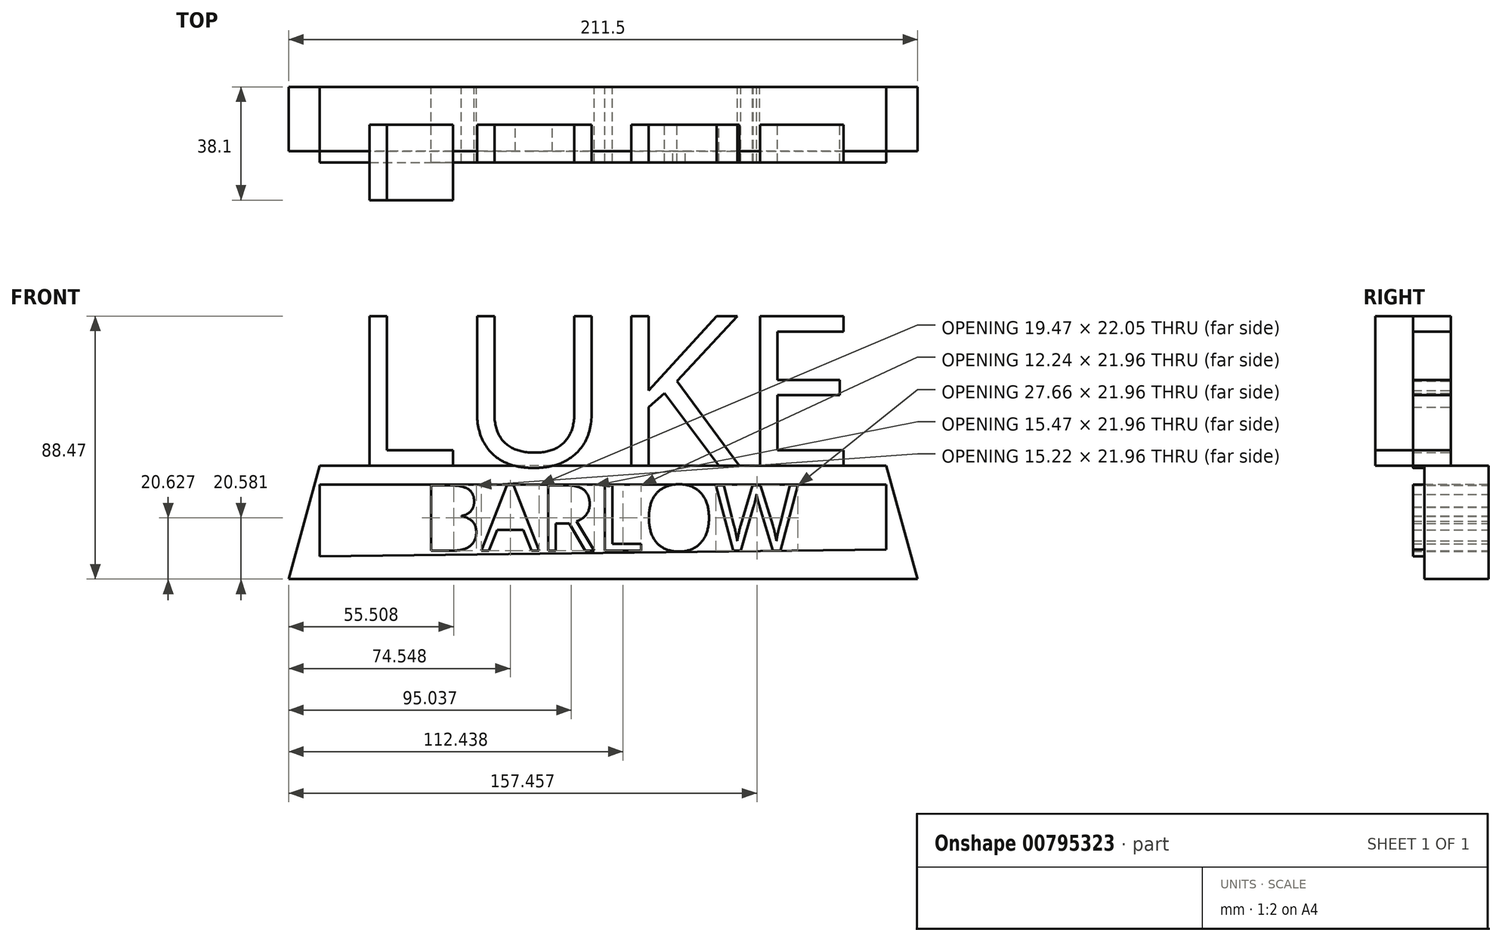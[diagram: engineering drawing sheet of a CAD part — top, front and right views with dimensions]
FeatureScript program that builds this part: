
annotation { "Feature Type Name" : "Feature", "Feature Type Description" : "" }
export const myFeature = defineFeature(function(context is Context, id is Id, definition is map)
    precondition{}
    {
        {
            var Q0;
            Q0=qCreatedBy(makeId("Front.planeOp"),FACE);
            var sketch = newSketch(context, id + "F0", { "sketchPlane" : qUnion([Q0])});
            skText(sketch, "E0", { "text": "LUKE\n", "fontName": "OpenSans-Regular.ttf"});
            skLineSegment(sketch, "E1.bottom", {"start": v(95.25, 0) * mm, "end": v(-95.25, 0) * mm});
            skLineSegment(sketch, "E1.top", {"start": v(95.25, -38.1) * mm, "end": v(-95.25, -38.1) * mm});
            skLineSegment(sketch, "E1.left", {"start": v(95.25, -6.35) * mm, "end": v(95.25, -28.18) * mm});
            skLineSegment(sketch, "E1.right", {"start": v(-95.25, -6.35) * mm, "end": v(-95.25, -30.4) * mm});
            skPoint(sketch, "E1.middle", {"position": v(0, -19.05) * mm});
            skLineSegment(sketch, "E2", {"start": v(-95.25, -6.35) * mm, "end": v(95.25, -6.35) * mm});
            skLineSegment(sketch, "E3.MirrorCS", {"start": v(-95.25, -30.4) * mm, "end": v(95.25, -28.18) * mm});
            skPoint(sketch, "E4.orphan", {"position": v(-95.25, -19.05) * mm});
            skPoint(sketch, "E5.end.orphan", {"position": v(95.25, -19.05) * mm});
            skLineSegment(sketch, "E6", {"start": v(-95.25, 0) * mm, "end": v(-105.75, -38.1) * mm});
            skLineSegment(sketch, "E7", {"start": v(-105.75, -38.1) * mm, "end": v(-95.25, -38.1) * mm});
            skLineSegment(sketch, "E8.MirrorCS", {"start": v(105.75, -38.1) * mm, "end": v(95.25, -38.1) * mm});
            skLineSegment(sketch, "E9.MirrorCS", {"start": v(95.25, 0) * mm, "end": v(105.75, -38.1) * mm});
            skText(sketch, "E10", { "text": "BARLOW", "fontName": "OpenSans-Regular.ttf"});
            const initialGuessF0  = {"E0": [-0.08543, 0, 1, 0, 0.0508], "E10": [-0.06087, -0.0285, 1, 0, 0.02215]};
            skSetInitialGuess(sketch, initialGuessF0);
            skSolve(sketch);
        }
        {
            var Q0;
            Q0=qSketchRegion(id+"F0",true);
            var Q1;
            Q1=makeQuery(id+"F0.imprint","IMPRINT",FACE,{"disambiguationData":[TD([[makeQuery(id+"F0.imprint","IMPRINT",EDGE,{"derivedFrom":sQuery(id+"F0.wireOp",EDGE,"63b13505-105a-406d-b1b1-810f40fcbeff.sketch_text.stroke-0")}),-1.0]])]});
            var Q2;
            {var subQ0=sQuery(id+"F0.wireOp",EDGE,"63b13505-105a-406d-b1b1-810f40fcbeff.sketch_text.stroke-1");Q2=makeQuery(id+"F0.imprint","IMPRINT",FACE,{"disambiguationData":[TD([[makeQuery(id+"F0.imprint","IMPRINT",EDGE,{"derivedFrom":subQ0}),1.0]])]});}
            var Q3;
            {var subQ29=sQuery(id+"F0.wireOp",EDGE,"E1.right");Q3=makeQuery(id+"F0.imprint","IMPRINT",FACE,{"disambiguationData":[TD([[makeQuery(id+"F0.imprint","IMPRINT",EDGE,{"derivedFrom":subQ29}),1.0]])]});}
            var Q4;
            {var subQ6=sQuery(id+"F0.wireOp",EDGE,"63b13505-105a-406d-b1b1-810f40fcbeff.sketch_text.stroke-29");Q4=makeQuery(id+"F0.imprint","IMPRINT",FACE,{"disambiguationData":[TD([[makeQuery(id+"F0.imprint","IMPRINT",EDGE,{"derivedFrom":subQ6}),-1.0]])]});}
            var Q5;
            {var subQ0=sQuery(id+"F0.wireOp",EDGE,"63b13505-105a-406d-b1b1-810f40fcbeff.sketch_text.stroke-31");var subQ1=sQuery(id+"F0.wireOp",EDGE,"E3.MirrorCS");var subQ2=makeQuery(id+"F0.imprint","INTERSECT",VERTEX,{"derivedFrom":[subQ1,subQ0]});Q5=makeQuery(id+"F0.imprint","IMPRINT",FACE,{"disambiguationData":[TD([[makeQuery(id+"F0.imprint","IMPRINT",EDGE,{"disambiguationData":[TD([[subQ2,-1.0]])],"derivedFrom":subQ1}),-1.0]])]});}
            var Q6;
            Q6=makeQuery(id+"F0.imprint","IMPRINT",FACE,{"disambiguationData":[TD([[makeQuery(id+"F0.imprint","IMPRINT",EDGE,{"derivedFrom":sQuery(id+"F0.wireOp",EDGE,"63b13505-105a-406d-b1b1-810f40fcbeff.sketch_text.stroke-38")}),1.0]])]});
            var Q7;
            Q7=makeQuery(id+"F0.imprint","IMPRINT",FACE,{"disambiguationData":[TD([[makeQuery(id+"F0.imprint","IMPRINT",EDGE,{"derivedFrom":sQuery(id+"F0.wireOp",EDGE,"63b13505-105a-406d-b1b1-810f40fcbeff.sketch_text.stroke-21")}),1.0]])]});
            var Q8;
            {var subQ6=sQuery(id+"F0.wireOp",EDGE,"63b13505-105a-406d-b1b1-810f40fcbeff.sketch_text.stroke-12");Q8=makeQuery(id+"F0.imprint","IMPRINT",FACE,{"disambiguationData":[TD([[makeQuery(id+"F0.imprint","IMPRINT",EDGE,{"derivedFrom":subQ6}),-1.0]])]});}
            var Q9;
            {var subQ0=sQuery(id+"F0.wireOp",EDGE,"63b13505-105a-406d-b1b1-810f40fcbeff.sketch_text.stroke-14");var subQ1=sQuery(id+"F0.wireOp",EDGE,"E3.MirrorCS");var subQ2=makeQuery(id+"F0.imprint","INTERSECT",VERTEX,{"derivedFrom":[subQ1,subQ0]});Q9=makeQuery(id+"F0.imprint","IMPRINT",FACE,{"disambiguationData":[TD([[makeQuery(id+"F0.imprint","IMPRINT",EDGE,{"disambiguationData":[TD([[subQ2,-1.0]])],"derivedFrom":subQ1}),-1.0]])]});}
            var Q10;
            Q10=makeQuery(id+"F0.imprint","IMPRINT",FACE,{"disambiguationData":[TD([[makeQuery(id+"F0.imprint","IMPRINT",EDGE,{"derivedFrom":sQuery(id+"F0.wireOp",EDGE,"63b13505-105a-406d-b1b1-810f40fcbeff.sketch_text.stroke-84")}),1.0]])]});
            var Q11;
            Q11=makeQuery(id+"F0.imprint","IMPRINT",FACE,{"disambiguationData":[TD([[makeQuery(id+"F0.imprint","IMPRINT",EDGE,{"derivedFrom":sQuery(id+"F0.wireOp",EDGE,"63b13505-105a-406d-b1b1-810f40fcbeff.sketch_text.stroke-46")}),-1.0]])]});
            var Q12;
            {var subQ5=sQuery(id+"F0.wireOp",EDGE,"63b13505-105a-406d-b1b1-810f40fcbeff.sketch_text.stroke-81");Q12=makeQuery(id+"F0.imprint","IMPRINT",FACE,{"disambiguationData":[TD([[makeQuery(id+"F0.imprint","IMPRINT",EDGE,{"derivedFrom":subQ5}),1.0]])]});}
            var Q13;
            Q13=makeQuery(id+"F0.imprint","IMPRINT",FACE,{"disambiguationData":[TD([[makeQuery(id+"F0.imprint","IMPRINT",EDGE,{"derivedFrom":sQuery(id+"F0.wireOp",EDGE,"63b13505-105a-406d-b1b1-810f40fcbeff.sketch_text.stroke-75")}),1.0]])]});
            var Q14;
            {var subQ11=sQuery(id+"F0.wireOp",EDGE,"63b13505-105a-406d-b1b1-810f40fcbeff.sketch_text.stroke-59");Q14=makeQuery(id+"F0.imprint","IMPRINT",FACE,{"disambiguationData":[TD([[makeQuery(id+"F0.imprint","IMPRINT",EDGE,{"derivedFrom":subQ11}),-1.0]])]});}
            var Q15;
            Q15=makeQuery(id+"F0.imprint","IMPRINT",FACE,{"disambiguationData":[TD([[makeQuery(id+"F0.imprint","IMPRINT",EDGE,{"derivedFrom":sQuery(id+"F0.wireOp",EDGE,"63b13505-105a-406d-b1b1-810f40fcbeff.sketch_text.stroke-104")}),1.0]])]});
            var Q16;
            {var subQ5=sQuery(id+"F0.wireOp",EDGE,"63b13505-105a-406d-b1b1-810f40fcbeff.sketch_text.stroke-91");Q16=makeQuery(id+"F0.imprint","IMPRINT",FACE,{"disambiguationData":[TD([[makeQuery(id+"F0.imprint","IMPRINT",EDGE,{"derivedFrom":subQ5}),-1.0]])]});}
            var Q17;
            {var subQ5=sQuery(id+"F0.wireOp",EDGE,"63b13505-105a-406d-b1b1-810f40fcbeff.sketch_text.stroke-103");Q17=makeQuery(id+"F0.imprint","IMPRINT",FACE,{"disambiguationData":[TD([[makeQuery(id+"F0.imprint","IMPRINT",EDGE,{"derivedFrom":subQ5}),-1.0]])]});}
            var Q18;
            {var subQ0=sQuery(id+"F0.wireOp",EDGE,"63b13505-105a-406d-b1b1-810f40fcbeff.sketch_text.stroke-109");Q18=makeQuery(id+"F0.imprint","IMPRINT",FACE,{"disambiguationData":[TD([[makeQuery(id+"F0.imprint","IMPRINT",EDGE,{"derivedFrom":subQ0}),1.0]])]});}
            var Q19;
            Q19=makeQuery(id+"F0.imprint","IMPRINT",FACE,{"disambiguationData":[TD([[makeQuery(id+"F0.imprint","IMPRINT",EDGE,{"derivedFrom":sQuery(id+"F0.wireOp",EDGE,"63b13505-105a-406d-b1b1-810f40fcbeff.sketch_text.stroke-109")}),-1.0]])]});
            var Q20;
            {var subQ9=sQuery(id+"F0.wireOp",EDGE,"63b13505-105a-406d-b1b1-810f40fcbeff.sketch_text.stroke-126");Q20=makeQuery(id+"F0.imprint","IMPRINT",FACE,{"disambiguationData":[TD([[makeQuery(id+"F0.imprint","IMPRINT",EDGE,{"derivedFrom":subQ9}),-1.0]])]});}
            var Q21;
            Q21=makeQuery(id+"F0.imprint","IMPRINT",FACE,{"disambiguationData":[TD([[makeQuery(id+"F0.imprint","IMPRINT",EDGE,{"derivedFrom":sQuery(id+"F0.wireOp",EDGE,"63b13505-105a-406d-b1b1-810f40fcbeff.sketch_text.stroke-141")}),1.0]])]});
            var Q22;
            {var subQ4=sQuery(id+"F0.wireOp",EDGE,"63b13505-105a-406d-b1b1-810f40fcbeff.sketch_text.stroke-126");Q22=makeQuery(id+"F0.imprint","IMPRINT",FACE,{"disambiguationData":[TD([[makeQuery(id+"F0.imprint","IMPRINT",EDGE,{"derivedFrom":subQ4}),1.0]])]});}
            var Q23;
            {var subQ5=sQuery(id+"F0.wireOp",EDGE,"63b13505-105a-406d-b1b1-810f40fcbeff.sketch_text.stroke-137");Q23=makeQuery(id+"F0.imprint","IMPRINT",FACE,{"disambiguationData":[TD([[makeQuery(id+"F0.imprint","IMPRINT",EDGE,{"derivedFrom":subQ5}),-1.0]])]});}
            var Q24;
            {var subQ0=sQuery(id+"F0.wireOp",EDGE,"63b13505-105a-406d-b1b1-810f40fcbeff.sketch_text.stroke-128");var subQ1=sQuery(id+"F0.wireOp",EDGE,"E3.MirrorCS");var subQ2=makeQuery(id+"F0.imprint","INTERSECT",VERTEX,{"derivedFrom":[subQ1,subQ0]});Q24=makeQuery(id+"F0.imprint","IMPRINT",FACE,{"disambiguationData":[TD([[makeQuery(id+"F0.imprint","IMPRINT",EDGE,{"disambiguationData":[TD([[subQ2,-1.0]])],"derivedFrom":subQ1}),-1.0]])]});}
            var Q25;
            Q25=makeQuery(id+"F0.imprint","IMPRINT",FACE,{"disambiguationData":[TD([[makeQuery(id+"F0.imprint","IMPRINT",EDGE,{"derivedFrom":sQuery(id+"F0.wireOp",EDGE,"63b13505-105a-406d-b1b1-810f40fcbeff.sketch_text.stroke-159")}),1.0]])]});
            var Q26;
            {var subQ6=sQuery(id+"F0.wireOp",EDGE,"63b13505-105a-406d-b1b1-810f40fcbeff.sketch_text.stroke-150");Q26=makeQuery(id+"F0.imprint","IMPRINT",FACE,{"disambiguationData":[TD([[makeQuery(id+"F0.imprint","IMPRINT",EDGE,{"derivedFrom":subQ6}),-1.0]])]});}
            var Q27;
            {var subQ3=sQuery(id+"F0.wireOp",EDGE,"E1.left");Q27=makeQuery(id+"F0.imprint","IMPRINT",FACE,{"disambiguationData":[TD([[makeQuery(id+"F0.imprint","IMPRINT",EDGE,{"derivedFrom":subQ3}),-1.0]])]});}
            var Q28;
            Q28=makeQuery(id+"F0.imprint","IMPRINT",FACE,{"disambiguationData":[TD([[makeQuery(id+"F0.imprint","IMPRINT",EDGE,{"derivedFrom":sQuery(id+"F0.wireOp",EDGE,"63b13505-105a-406d-b1b1-810f40fcbeff.sketch_text.stroke-176")}),1.0]])]});
            var Q29;
            {var subQ6=sQuery(id+"F0.wireOp",EDGE,"63b13505-105a-406d-b1b1-810f40fcbeff.sketch_text.stroke-167");Q29=makeQuery(id+"F0.imprint","IMPRINT",FACE,{"disambiguationData":[TD([[makeQuery(id+"F0.imprint","IMPRINT",EDGE,{"derivedFrom":subQ6}),-1.0]])]});}
            var Q30;
            {var subQ0=sQuery(id+"F0.wireOp",EDGE,"63b13505-105a-406d-b1b1-810f40fcbeff.sketch_text.stroke-169");var subQ1=sQuery(id+"F0.wireOp",EDGE,"E3.MirrorCS");var subQ2=makeQuery(id+"F0.imprint","INTERSECT",VERTEX,{"derivedFrom":[subQ1,subQ0]});Q30=makeQuery(id+"F0.imprint","IMPRINT",FACE,{"disambiguationData":[TD([[makeQuery(id+"F0.imprint","IMPRINT",EDGE,{"disambiguationData":[TD([[subQ2,-1.0]])],"derivedFrom":subQ1}),-1.0]])]});}
            var Q31;
            {var subQ0=sQuery(id+"F0.wireOp",EDGE,"63b13505-105a-406d-b1b1-810f40fcbeff.sketch_text.stroke-152");var subQ1=sQuery(id+"F0.wireOp",EDGE,"E3.MirrorCS");var subQ2=makeQuery(id+"F0.imprint","INTERSECT",VERTEX,{"derivedFrom":[subQ1,subQ0]});Q31=makeQuery(id+"F0.imprint","IMPRINT",FACE,{"disambiguationData":[TD([[makeQuery(id+"F0.imprint","IMPRINT",EDGE,{"disambiguationData":[TD([[subQ2,-1.0]])],"derivedFrom":subQ1}),-1.0]])]});}
            var Q32;
            Q32=makeQuery(id+"F0.imprint","IMPRINT",FACE,{"disambiguationData":[TD([[makeQuery(id+"F0.imprint","IMPRINT",EDGE,{"derivedFrom":sQuery(id+"F0.wireOp",EDGE,"63b13505-105a-406d-b1b1-810f40fcbeff.sketch_text.stroke-184")}),-1.0]])]});
            var Q33;
            {var subQ0=sQuery(id+"F0.wireOp",EDGE,"63b13505-105a-406d-b1b1-810f40fcbeff.sketch_text.stroke-197");Q33=makeQuery(id+"F0.imprint","IMPRINT",FACE,{"disambiguationData":[TD([[makeQuery(id+"F0.imprint","IMPRINT",EDGE,{"derivedFrom":subQ0}),1.0]])]});}
            var Q34;
            Q34=makeQuery(id+"F0.imprint","IMPRINT",FACE,{"disambiguationData":[TD([[makeQuery(id+"F0.imprint","IMPRINT",EDGE,{"derivedFrom":sQuery(id+"F0.wireOp",EDGE,"63b13505-105a-406d-b1b1-810f40fcbeff.sketch_text.stroke-197")}),-1.0]])]});
            extrude(context, id + "F1", {"entities" : qUnion([Q0, Q1, Q2, Q3, Q4, Q5, Q6, Q7, Q8, Q9, Q10, Q11, Q12, Q13, Q14, Q15, Q16, Q17, Q18, Q19, Q20, Q21, Q22, Q23, Q24, Q25, Q26, Q27, Q28, Q29, Q30, Q31, Q32, Q33, Q34]), "depth" : 25.4 * mm, "offsetDistance" : 25.4 * mm});
        }
        {
            var Q0;
            {var subQ6=sQuery(id+"F0.wireOp",EDGE,"63b13505-105a-406d-b1b1-810f40fcbeff.sketch_text.stroke-12");Q0=makeQuery(id+"F0.imprint","IMPRINT",FACE,{"disambiguationData":[TD([[makeQuery(id+"F0.imprint","IMPRINT",EDGE,{"derivedFrom":subQ6}),-1.0]])]});}
            var Q1;
            Q1=makeQuery(id+"F0.imprint","IMPRINT",FACE,{"disambiguationData":[TD([[makeQuery(id+"F0.imprint","IMPRINT",EDGE,{"derivedFrom":sQuery(id+"F0.wireOp",EDGE,"63b13505-105a-406d-b1b1-810f40fcbeff.sketch_text.stroke-0")}),-1.0]])]});
            var Q2;
            {var subQ0=sQuery(id+"F0.wireOp",EDGE,"63b13505-105a-406d-b1b1-810f40fcbeff.sketch_text.stroke-14");var subQ1=sQuery(id+"F0.wireOp",EDGE,"E3.MirrorCS");var subQ2=makeQuery(id+"F0.imprint","INTERSECT",VERTEX,{"derivedFrom":[subQ1,subQ0]});Q2=makeQuery(id+"F0.imprint","IMPRINT",FACE,{"disambiguationData":[TD([[makeQuery(id+"F0.imprint","IMPRINT",EDGE,{"disambiguationData":[TD([[subQ2,-1.0]])],"derivedFrom":subQ1}),-1.0]])]});}
            var Q3;
            {var subQ6=sQuery(id+"F0.wireOp",EDGE,"63b13505-105a-406d-b1b1-810f40fcbeff.sketch_text.stroke-29");Q3=makeQuery(id+"F0.imprint","IMPRINT",FACE,{"disambiguationData":[TD([[makeQuery(id+"F0.imprint","IMPRINT",EDGE,{"derivedFrom":subQ6}),-1.0]])]});}
            var Q4;
            {var subQ0=sQuery(id+"F0.wireOp",EDGE,"63b13505-105a-406d-b1b1-810f40fcbeff.sketch_text.stroke-31");var subQ1=sQuery(id+"F0.wireOp",EDGE,"E3.MirrorCS");var subQ2=makeQuery(id+"F0.imprint","INTERSECT",VERTEX,{"derivedFrom":[subQ1,subQ0]});Q4=makeQuery(id+"F0.imprint","IMPRINT",FACE,{"disambiguationData":[TD([[makeQuery(id+"F0.imprint","IMPRINT",EDGE,{"disambiguationData":[TD([[subQ2,-1.0]])],"derivedFrom":subQ1}),-1.0]])]});}
            var Q5;
            {var subQ11=sQuery(id+"F0.wireOp",EDGE,"63b13505-105a-406d-b1b1-810f40fcbeff.sketch_text.stroke-59");Q5=makeQuery(id+"F0.imprint","IMPRINT",FACE,{"disambiguationData":[TD([[makeQuery(id+"F0.imprint","IMPRINT",EDGE,{"derivedFrom":subQ11}),-1.0]])]});}
            var Q6;
            Q6=makeQuery(id+"F0.imprint","IMPRINT",FACE,{"disambiguationData":[TD([[makeQuery(id+"F0.imprint","IMPRINT",EDGE,{"derivedFrom":sQuery(id+"F0.wireOp",EDGE,"63b13505-105a-406d-b1b1-810f40fcbeff.sketch_text.stroke-46")}),-1.0]])]});
            var Q7;
            {var subQ5=sQuery(id+"F0.wireOp",EDGE,"63b13505-105a-406d-b1b1-810f40fcbeff.sketch_text.stroke-91");Q7=makeQuery(id+"F0.imprint","IMPRINT",FACE,{"disambiguationData":[TD([[makeQuery(id+"F0.imprint","IMPRINT",EDGE,{"derivedFrom":subQ5}),-1.0]])]});}
            var Q8;
            Q8=makeQuery(id+"F0.imprint","IMPRINT",FACE,{"disambiguationData":[TD([[makeQuery(id+"F0.imprint","IMPRINT",EDGE,{"derivedFrom":sQuery(id+"F0.wireOp",EDGE,"63b13505-105a-406d-b1b1-810f40fcbeff.sketch_text.stroke-109")}),-1.0]])]});
            var Q9;
            {var subQ9=sQuery(id+"F0.wireOp",EDGE,"63b13505-105a-406d-b1b1-810f40fcbeff.sketch_text.stroke-126");Q9=makeQuery(id+"F0.imprint","IMPRINT",FACE,{"disambiguationData":[TD([[makeQuery(id+"F0.imprint","IMPRINT",EDGE,{"derivedFrom":subQ9}),-1.0]])]});}
            var Q10;
            {var subQ5=sQuery(id+"F0.wireOp",EDGE,"63b13505-105a-406d-b1b1-810f40fcbeff.sketch_text.stroke-137");Q10=makeQuery(id+"F0.imprint","IMPRINT",FACE,{"disambiguationData":[TD([[makeQuery(id+"F0.imprint","IMPRINT",EDGE,{"derivedFrom":subQ5}),-1.0]])]});}
            var Q11;
            {var subQ0=sQuery(id+"F0.wireOp",EDGE,"63b13505-105a-406d-b1b1-810f40fcbeff.sketch_text.stroke-128");var subQ1=sQuery(id+"F0.wireOp",EDGE,"E3.MirrorCS");var subQ2=makeQuery(id+"F0.imprint","INTERSECT",VERTEX,{"derivedFrom":[subQ1,subQ0]});Q11=makeQuery(id+"F0.imprint","IMPRINT",FACE,{"disambiguationData":[TD([[makeQuery(id+"F0.imprint","IMPRINT",EDGE,{"disambiguationData":[TD([[subQ2,-1.0]])],"derivedFrom":subQ1}),-1.0]])]});}
            var Q12;
            {var subQ5=sQuery(id+"F0.wireOp",EDGE,"63b13505-105a-406d-b1b1-810f40fcbeff.sketch_text.stroke-103");Q12=makeQuery(id+"F0.imprint","IMPRINT",FACE,{"disambiguationData":[TD([[makeQuery(id+"F0.imprint","IMPRINT",EDGE,{"derivedFrom":subQ5}),-1.0]])]});}
            var Q13;
            {var subQ6=sQuery(id+"F0.wireOp",EDGE,"63b13505-105a-406d-b1b1-810f40fcbeff.sketch_text.stroke-150");Q13=makeQuery(id+"F0.imprint","IMPRINT",FACE,{"disambiguationData":[TD([[makeQuery(id+"F0.imprint","IMPRINT",EDGE,{"derivedFrom":subQ6}),-1.0]])]});}
            var Q14;
            {var subQ0=sQuery(id+"F0.wireOp",EDGE,"63b13505-105a-406d-b1b1-810f40fcbeff.sketch_text.stroke-152");var subQ1=sQuery(id+"F0.wireOp",EDGE,"E3.MirrorCS");var subQ2=makeQuery(id+"F0.imprint","INTERSECT",VERTEX,{"derivedFrom":[subQ1,subQ0]});Q14=makeQuery(id+"F0.imprint","IMPRINT",FACE,{"disambiguationData":[TD([[makeQuery(id+"F0.imprint","IMPRINT",EDGE,{"disambiguationData":[TD([[subQ2,-1.0]])],"derivedFrom":subQ1}),-1.0]])]});}
            var Q15;
            {var subQ6=sQuery(id+"F0.wireOp",EDGE,"63b13505-105a-406d-b1b1-810f40fcbeff.sketch_text.stroke-167");Q15=makeQuery(id+"F0.imprint","IMPRINT",FACE,{"disambiguationData":[TD([[makeQuery(id+"F0.imprint","IMPRINT",EDGE,{"derivedFrom":subQ6}),-1.0]])]});}
            var Q16;
            {var subQ0=sQuery(id+"F0.wireOp",EDGE,"63b13505-105a-406d-b1b1-810f40fcbeff.sketch_text.stroke-169");var subQ1=sQuery(id+"F0.wireOp",EDGE,"E3.MirrorCS");var subQ2=makeQuery(id+"F0.imprint","INTERSECT",VERTEX,{"derivedFrom":[subQ1,subQ0]});Q16=makeQuery(id+"F0.imprint","IMPRINT",FACE,{"disambiguationData":[TD([[makeQuery(id+"F0.imprint","IMPRINT",EDGE,{"disambiguationData":[TD([[subQ2,-1.0]])],"derivedFrom":subQ1}),-1.0]])]});}
            var Q17;
            Q17=makeQuery(id+"F0.imprint","IMPRINT",FACE,{"disambiguationData":[TD([[makeQuery(id+"F0.imprint","IMPRINT",EDGE,{"derivedFrom":sQuery(id+"F0.wireOp",EDGE,"63b13505-105a-406d-b1b1-810f40fcbeff.sketch_text.stroke-184")}),-1.0]])]});
            var Q18;
            Q18=makeQuery(id+"F0.imprint","IMPRINT",FACE,{"disambiguationData":[TD([[makeQuery(id+"F0.imprint","IMPRINT",EDGE,{"derivedFrom":sQuery(id+"F0.wireOp",EDGE,"63b13505-105a-406d-b1b1-810f40fcbeff.sketch_text.stroke-197")}),-1.0]])]});
            extrude(context, id + "F2", {"entities" : qUnion([Q0, Q1, Q2, Q3, Q4, Q5, Q6, Q7, Q8, Q9, Q10, Q11, Q12, Q13, Q14, Q15, Q16, Q17, Q18]), "operationType" : NewBodyOperationType.REMOVE, "depth" : 25.4 * mm, "offsetDistance" : 25.4 * mm, "hasSecondDirection" : true, "secondDirectionOppositeDirection" : false, "secondDirectionDepth" : 21.59 * mm});
        }
        {
            var Q0;
            {var subQ0=sQuery(id+"F0.wireOp",EDGE,"E9.MirrorCS");var subQ1=sQuery(id+"F0.wireOp",EDGE,"E6");var subQ2=sQuery(id+"F0.wireOp",EDGE,"E8.MirrorCS");var subQ3=sQuery(id+"F0.wireOp",EDGE,"E7");var subQ4=sQuery(id+"F0.wireOp",EDGE,"E1.top");var subQ5=sQuery(id+"F0.wireOp",EDGE,"E1.bottom");var subQ6=sQuery(id+"F0.wireOp",EDGE,"E0.sketch_text.stroke-0");var subQ7=sQuery(id+"F0.wireOp",EDGE,"E0.sketch_text.stroke-21");var subQ8=sQuery(id+"F0.wireOp",EDGE,"E0.sketch_text.stroke-23");var subQ9=sQuery(id+"F0.wireOp",EDGE,"E0.sketch_text.stroke-36");var subQ10=sQuery(id+"F0.wireOp",EDGE,"E0.sketch_text.stroke-35");var subQ11=sQuery(id+"F0.wireOp",EDGE,"E0.sketch_text.stroke-34");var subQ12=sQuery(id+"F0.wireOp",EDGE,"E0.sketch_text.stroke-33");var subQ13=sQuery(id+"F0.wireOp",EDGE,"E0.sketch_text.stroke-31");var subQ14=sQuery(id+"F0.wireOp",EDGE,"E0.sketch_text.stroke-30");var subQ15=sQuery(id+"F0.wireOp",EDGE,"E0.sketch_text.stroke-29");var subQ16=sQuery(id+"F0.wireOp",EDGE,"E0.sketch_text.stroke-28");var subQ17=sQuery(id+"F0.wireOp",EDGE,"E0.sketch_text.stroke-27");var subQ18=sQuery(id+"F0.wireOp",EDGE,"E0.sketch_text.stroke-26");var subQ19=sQuery(id+"F0.wireOp",EDGE,"E0.sketch_text.stroke-25");var subQ20=sQuery(id+"F0.wireOp",EDGE,"E0.sketch_text.stroke-22");var subQ21=sQuery(id+"F0.wireOp",EDGE,"E0.sketch_text.stroke-17");var subQ22=sQuery(id+"F0.wireOp",EDGE,"E0.sketch_text.stroke-16");var subQ23=sQuery(id+"F0.wireOp",EDGE,"E0.sketch_text.stroke-15");var subQ24=sQuery(id+"F0.wireOp",EDGE,"E0.sketch_text.stroke-14");var subQ25=sQuery(id+"F0.wireOp",EDGE,"E0.sketch_text.stroke-13");var subQ26=sQuery(id+"F0.wireOp",EDGE,"E0.sketch_text.stroke-12");var subQ27=sQuery(id+"F0.wireOp",EDGE,"E0.sketch_text.stroke-11");var subQ28=sQuery(id+"F0.wireOp",EDGE,"E0.sketch_text.stroke-10");var subQ29=sQuery(id+"F0.wireOp",EDGE,"E0.sketch_text.stroke-9");var subQ30=sQuery(id+"F0.wireOp",EDGE,"E0.sketch_text.stroke-8");var subQ31=sQuery(id+"F0.wireOp",EDGE,"E0.sketch_text.stroke-7");var subQ32=sQuery(id+"F0.wireOp",EDGE,"E0.sketch_text.stroke-6");var subQ33=sQuery(id+"F0.wireOp",EDGE,"E0.sketch_text.stroke-4");var subQ34=sQuery(id+"F0.wireOp",EDGE,"E0.sketch_text.stroke-3");var subQ35=sQuery(id+"F0.wireOp",EDGE,"E0.sketch_text.stroke-2");var subQ36=sQuery(id+"F0.wireOp",EDGE,"E0.sketch_text.stroke-1");var subQ37=sQuery(id+"F0.wireOp",EDGE,"E0.sketch_text.stroke-43");var subQ38=sQuery(id+"F0.wireOp",EDGE,"E0.sketch_text.stroke-42");var subQ39=sQuery(id+"F0.wireOp",EDGE,"E0.sketch_text.stroke-41");var subQ40=sQuery(id+"F0.wireOp",EDGE,"E0.sketch_text.stroke-40");var subQ41=sQuery(id+"F0.wireOp",EDGE,"E0.sketch_text.stroke-39");var subQ42=sQuery(id+"F0.wireOp",EDGE,"E0.sketch_text.stroke-38");var subQ43=sQuery(id+"F0.wireOp",EDGE,"E0.sketch_text.stroke-37");var subQ44=sQuery(id+"F0.wireOp",EDGE,"E0.sketch_text.stroke-18");var subQ45=sQuery(id+"F0.wireOp",EDGE,"E0.sketch_text.stroke-19");Q0=makeQuery(id+"F2.boolean.opBoolean","SPLIT",FACE,{"disambiguationData":[TD([makeQuery(id+"F1.opExtrude","SWEPT_FACE",FACE,{"disambiguationData":[OSD([subQ6])]})])],"derivedFrom":makeQuery(id+"F1.opExtrude","CAP_FACE",FACE,{"disambiguationData":[OSD([subQ6,subQ36,subQ35,subQ34,subQ33,subQ32,subQ31,subQ30,subQ29,subQ28,subQ27,subQ26,subQ25,subQ24,subQ23,subQ22,subQ21,subQ44,subQ45,subQ7,subQ20,subQ8,subQ19,subQ18,subQ17,subQ16,subQ15,subQ14,subQ13,subQ12,subQ11,subQ10,subQ9,subQ43,subQ42,subQ41,subQ40,subQ39,subQ38,subQ37,subQ5,subQ4,subQ1,subQ3,subQ2,subQ0])],"isStart":false})});}
            var Q1;
            Q1=makeQuery(id+"F2.boolean.opBoolean","SPLIT",FACE,{"disambiguationData":[TD([makeQuery(id+"F2.opExtrude","SWEPT_FACE",FACE,{"disambiguationData":[OSD([sQuery(id+"F0.wireOp",EDGE,"63b13505-105a-406d-b1b1-810f40fcbeff.sketch_text.stroke-21")])]})])],"derivedFrom":makeQuery(id+"F1.opExtrude","CAP_FACE",FACE,{"disambiguationData":[OSD([sQuery(id+"F0.wireOp",EDGE,"E0.sketch_text.stroke-0"),sQuery(id+"F0.wireOp",EDGE,"E0.sketch_text.stroke-1"),sQuery(id+"F0.wireOp",EDGE,"E0.sketch_text.stroke-2"),sQuery(id+"F0.wireOp",EDGE,"E0.sketch_text.stroke-3"),sQuery(id+"F0.wireOp",EDGE,"E0.sketch_text.stroke-4"),sQuery(id+"F0.wireOp",EDGE,"E0.sketch_text.stroke-6"),sQuery(id+"F0.wireOp",EDGE,"E0.sketch_text.stroke-7"),sQuery(id+"F0.wireOp",EDGE,"E0.sketch_text.stroke-8"),sQuery(id+"F0.wireOp",EDGE,"E0.sketch_text.stroke-9"),sQuery(id+"F0.wireOp",EDGE,"E0.sketch_text.stroke-10"),sQuery(id+"F0.wireOp",EDGE,"E0.sketch_text.stroke-11"),sQuery(id+"F0.wireOp",EDGE,"E0.sketch_text.stroke-12"),sQuery(id+"F0.wireOp",EDGE,"E0.sketch_text.stroke-13"),sQuery(id+"F0.wireOp",EDGE,"E0.sketch_text.stroke-14"),sQuery(id+"F0.wireOp",EDGE,"E0.sketch_text.stroke-15"),sQuery(id+"F0.wireOp",EDGE,"E0.sketch_text.stroke-16"),sQuery(id+"F0.wireOp",EDGE,"E0.sketch_text.stroke-17"),sQuery(id+"F0.wireOp",EDGE,"E0.sketch_text.stroke-18"),sQuery(id+"F0.wireOp",EDGE,"E0.sketch_text.stroke-19"),sQuery(id+"F0.wireOp",EDGE,"E0.sketch_text.stroke-21"),sQuery(id+"F0.wireOp",EDGE,"E0.sketch_text.stroke-22"),sQuery(id+"F0.wireOp",EDGE,"E0.sketch_text.stroke-23"),sQuery(id+"F0.wireOp",EDGE,"E0.sketch_text.stroke-25"),sQuery(id+"F0.wireOp",EDGE,"E0.sketch_text.stroke-26"),sQuery(id+"F0.wireOp",EDGE,"E0.sketch_text.stroke-27"),sQuery(id+"F0.wireOp",EDGE,"E0.sketch_text.stroke-28"),sQuery(id+"F0.wireOp",EDGE,"E0.sketch_text.stroke-29"),sQuery(id+"F0.wireOp",EDGE,"E0.sketch_text.stroke-30"),sQuery(id+"F0.wireOp",EDGE,"E0.sketch_text.stroke-31"),sQuery(id+"F0.wireOp",EDGE,"E0.sketch_text.stroke-33"),sQuery(id+"F0.wireOp",EDGE,"E0.sketch_text.stroke-34"),sQuery(id+"F0.wireOp",EDGE,"E0.sketch_text.stroke-35"),sQuery(id+"F0.wireOp",EDGE,"E0.sketch_text.stroke-36"),sQuery(id+"F0.wireOp",EDGE,"E0.sketch_text.stroke-37"),sQuery(id+"F0.wireOp",EDGE,"E0.sketch_text.stroke-38"),sQuery(id+"F0.wireOp",EDGE,"E0.sketch_text.stroke-39"),sQuery(id+"F0.wireOp",EDGE,"E0.sketch_text.stroke-40"),sQuery(id+"F0.wireOp",EDGE,"E0.sketch_text.stroke-41"),sQuery(id+"F0.wireOp",EDGE,"E0.sketch_text.stroke-42"),sQuery(id+"F0.wireOp",EDGE,"E0.sketch_text.stroke-43"),sQuery(id+"F0.wireOp",EDGE,"E1.bottom"),sQuery(id+"F0.wireOp",EDGE,"E1.top"),sQuery(id+"F0.wireOp",EDGE,"E6"),sQuery(id+"F0.wireOp",EDGE,"E7"),sQuery(id+"F0.wireOp",EDGE,"E8.MirrorCS"),sQuery(id+"F0.wireOp",EDGE,"E9.MirrorCS")])],"isStart":false})});
            var Q2;
            Q2=makeQuery(id+"F2.boolean.opBoolean","SPLIT",FACE,{"disambiguationData":[TD([makeQuery(id+"F2.opExtrude","SWEPT_FACE",FACE,{"disambiguationData":[OSD([sQuery(id+"F0.wireOp",EDGE,"63b13505-105a-406d-b1b1-810f40fcbeff.sketch_text.stroke-38")])]})])],"derivedFrom":makeQuery(id+"F1.opExtrude","CAP_FACE",FACE,{"disambiguationData":[OSD([sQuery(id+"F0.wireOp",EDGE,"E0.sketch_text.stroke-0"),sQuery(id+"F0.wireOp",EDGE,"E0.sketch_text.stroke-1"),sQuery(id+"F0.wireOp",EDGE,"E0.sketch_text.stroke-2"),sQuery(id+"F0.wireOp",EDGE,"E0.sketch_text.stroke-3"),sQuery(id+"F0.wireOp",EDGE,"E0.sketch_text.stroke-4"),sQuery(id+"F0.wireOp",EDGE,"E0.sketch_text.stroke-6"),sQuery(id+"F0.wireOp",EDGE,"E0.sketch_text.stroke-7"),sQuery(id+"F0.wireOp",EDGE,"E0.sketch_text.stroke-8"),sQuery(id+"F0.wireOp",EDGE,"E0.sketch_text.stroke-9"),sQuery(id+"F0.wireOp",EDGE,"E0.sketch_text.stroke-10"),sQuery(id+"F0.wireOp",EDGE,"E0.sketch_text.stroke-11"),sQuery(id+"F0.wireOp",EDGE,"E0.sketch_text.stroke-12"),sQuery(id+"F0.wireOp",EDGE,"E0.sketch_text.stroke-13"),sQuery(id+"F0.wireOp",EDGE,"E0.sketch_text.stroke-14"),sQuery(id+"F0.wireOp",EDGE,"E0.sketch_text.stroke-15"),sQuery(id+"F0.wireOp",EDGE,"E0.sketch_text.stroke-16"),sQuery(id+"F0.wireOp",EDGE,"E0.sketch_text.stroke-17"),sQuery(id+"F0.wireOp",EDGE,"E0.sketch_text.stroke-18"),sQuery(id+"F0.wireOp",EDGE,"E0.sketch_text.stroke-19"),sQuery(id+"F0.wireOp",EDGE,"E0.sketch_text.stroke-21"),sQuery(id+"F0.wireOp",EDGE,"E0.sketch_text.stroke-22"),sQuery(id+"F0.wireOp",EDGE,"E0.sketch_text.stroke-23"),sQuery(id+"F0.wireOp",EDGE,"E0.sketch_text.stroke-25"),sQuery(id+"F0.wireOp",EDGE,"E0.sketch_text.stroke-26"),sQuery(id+"F0.wireOp",EDGE,"E0.sketch_text.stroke-27"),sQuery(id+"F0.wireOp",EDGE,"E0.sketch_text.stroke-28"),sQuery(id+"F0.wireOp",EDGE,"E0.sketch_text.stroke-29"),sQuery(id+"F0.wireOp",EDGE,"E0.sketch_text.stroke-30"),sQuery(id+"F0.wireOp",EDGE,"E0.sketch_text.stroke-31"),sQuery(id+"F0.wireOp",EDGE,"E0.sketch_text.stroke-33"),sQuery(id+"F0.wireOp",EDGE,"E0.sketch_text.stroke-34"),sQuery(id+"F0.wireOp",EDGE,"E0.sketch_text.stroke-35"),sQuery(id+"F0.wireOp",EDGE,"E0.sketch_text.stroke-36"),sQuery(id+"F0.wireOp",EDGE,"E0.sketch_text.stroke-37"),sQuery(id+"F0.wireOp",EDGE,"E0.sketch_text.stroke-38"),sQuery(id+"F0.wireOp",EDGE,"E0.sketch_text.stroke-39"),sQuery(id+"F0.wireOp",EDGE,"E0.sketch_text.stroke-40"),sQuery(id+"F0.wireOp",EDGE,"E0.sketch_text.stroke-41"),sQuery(id+"F0.wireOp",EDGE,"E0.sketch_text.stroke-42"),sQuery(id+"F0.wireOp",EDGE,"E0.sketch_text.stroke-43"),sQuery(id+"F0.wireOp",EDGE,"E1.bottom"),sQuery(id+"F0.wireOp",EDGE,"E1.top"),sQuery(id+"F0.wireOp",EDGE,"E6"),sQuery(id+"F0.wireOp",EDGE,"E7"),sQuery(id+"F0.wireOp",EDGE,"E8.MirrorCS"),sQuery(id+"F0.wireOp",EDGE,"E9.MirrorCS")])],"isStart":false})});
            var Q3;
            Q3=makeQuery(id+"F2.boolean.opBoolean","SPLIT",FACE,{"disambiguationData":[TD([makeQuery(id+"F2.opExtrude","SWEPT_FACE",FACE,{"disambiguationData":[OSD([sQuery(id+"F0.wireOp",EDGE,"63b13505-105a-406d-b1b1-810f40fcbeff.sketch_text.stroke-84")])]})])],"derivedFrom":makeQuery(id+"F1.opExtrude","CAP_FACE",FACE,{"disambiguationData":[OSD([sQuery(id+"F0.wireOp",EDGE,"E0.sketch_text.stroke-0"),sQuery(id+"F0.wireOp",EDGE,"E0.sketch_text.stroke-1"),sQuery(id+"F0.wireOp",EDGE,"E0.sketch_text.stroke-2"),sQuery(id+"F0.wireOp",EDGE,"E0.sketch_text.stroke-3"),sQuery(id+"F0.wireOp",EDGE,"E0.sketch_text.stroke-4"),sQuery(id+"F0.wireOp",EDGE,"E0.sketch_text.stroke-6"),sQuery(id+"F0.wireOp",EDGE,"E0.sketch_text.stroke-7"),sQuery(id+"F0.wireOp",EDGE,"E0.sketch_text.stroke-8"),sQuery(id+"F0.wireOp",EDGE,"E0.sketch_text.stroke-9"),sQuery(id+"F0.wireOp",EDGE,"E0.sketch_text.stroke-10"),sQuery(id+"F0.wireOp",EDGE,"E0.sketch_text.stroke-11"),sQuery(id+"F0.wireOp",EDGE,"E0.sketch_text.stroke-12"),sQuery(id+"F0.wireOp",EDGE,"E0.sketch_text.stroke-13"),sQuery(id+"F0.wireOp",EDGE,"E0.sketch_text.stroke-14"),sQuery(id+"F0.wireOp",EDGE,"E0.sketch_text.stroke-15"),sQuery(id+"F0.wireOp",EDGE,"E0.sketch_text.stroke-16"),sQuery(id+"F0.wireOp",EDGE,"E0.sketch_text.stroke-17"),sQuery(id+"F0.wireOp",EDGE,"E0.sketch_text.stroke-18"),sQuery(id+"F0.wireOp",EDGE,"E0.sketch_text.stroke-19"),sQuery(id+"F0.wireOp",EDGE,"E0.sketch_text.stroke-21"),sQuery(id+"F0.wireOp",EDGE,"E0.sketch_text.stroke-22"),sQuery(id+"F0.wireOp",EDGE,"E0.sketch_text.stroke-23"),sQuery(id+"F0.wireOp",EDGE,"E0.sketch_text.stroke-25"),sQuery(id+"F0.wireOp",EDGE,"E0.sketch_text.stroke-26"),sQuery(id+"F0.wireOp",EDGE,"E0.sketch_text.stroke-27"),sQuery(id+"F0.wireOp",EDGE,"E0.sketch_text.stroke-28"),sQuery(id+"F0.wireOp",EDGE,"E0.sketch_text.stroke-29"),sQuery(id+"F0.wireOp",EDGE,"E0.sketch_text.stroke-30"),sQuery(id+"F0.wireOp",EDGE,"E0.sketch_text.stroke-31"),sQuery(id+"F0.wireOp",EDGE,"E0.sketch_text.stroke-33"),sQuery(id+"F0.wireOp",EDGE,"E0.sketch_text.stroke-34"),sQuery(id+"F0.wireOp",EDGE,"E0.sketch_text.stroke-35"),sQuery(id+"F0.wireOp",EDGE,"E0.sketch_text.stroke-36"),sQuery(id+"F0.wireOp",EDGE,"E0.sketch_text.stroke-37"),sQuery(id+"F0.wireOp",EDGE,"E0.sketch_text.stroke-38"),sQuery(id+"F0.wireOp",EDGE,"E0.sketch_text.stroke-39"),sQuery(id+"F0.wireOp",EDGE,"E0.sketch_text.stroke-40"),sQuery(id+"F0.wireOp",EDGE,"E0.sketch_text.stroke-41"),sQuery(id+"F0.wireOp",EDGE,"E0.sketch_text.stroke-42"),sQuery(id+"F0.wireOp",EDGE,"E0.sketch_text.stroke-43"),sQuery(id+"F0.wireOp",EDGE,"E1.bottom"),sQuery(id+"F0.wireOp",EDGE,"E1.top"),sQuery(id+"F0.wireOp",EDGE,"E6"),sQuery(id+"F0.wireOp",EDGE,"E7"),sQuery(id+"F0.wireOp",EDGE,"E8.MirrorCS"),sQuery(id+"F0.wireOp",EDGE,"E9.MirrorCS")])],"isStart":false})});
            var Q4;
            Q4=makeQuery(id+"F2.boolean.opBoolean","SPLIT",FACE,{"disambiguationData":[TD([makeQuery(id+"F2.opExtrude","SWEPT_FACE",FACE,{"disambiguationData":[OSD([sQuery(id+"F0.wireOp",EDGE,"63b13505-105a-406d-b1b1-810f40fcbeff.sketch_text.stroke-75")])]})])],"derivedFrom":makeQuery(id+"F1.opExtrude","CAP_FACE",FACE,{"disambiguationData":[OSD([sQuery(id+"F0.wireOp",EDGE,"E0.sketch_text.stroke-0"),sQuery(id+"F0.wireOp",EDGE,"E0.sketch_text.stroke-1"),sQuery(id+"F0.wireOp",EDGE,"E0.sketch_text.stroke-2"),sQuery(id+"F0.wireOp",EDGE,"E0.sketch_text.stroke-3"),sQuery(id+"F0.wireOp",EDGE,"E0.sketch_text.stroke-4"),sQuery(id+"F0.wireOp",EDGE,"E0.sketch_text.stroke-6"),sQuery(id+"F0.wireOp",EDGE,"E0.sketch_text.stroke-7"),sQuery(id+"F0.wireOp",EDGE,"E0.sketch_text.stroke-8"),sQuery(id+"F0.wireOp",EDGE,"E0.sketch_text.stroke-9"),sQuery(id+"F0.wireOp",EDGE,"E0.sketch_text.stroke-10"),sQuery(id+"F0.wireOp",EDGE,"E0.sketch_text.stroke-11"),sQuery(id+"F0.wireOp",EDGE,"E0.sketch_text.stroke-12"),sQuery(id+"F0.wireOp",EDGE,"E0.sketch_text.stroke-13"),sQuery(id+"F0.wireOp",EDGE,"E0.sketch_text.stroke-14"),sQuery(id+"F0.wireOp",EDGE,"E0.sketch_text.stroke-15"),sQuery(id+"F0.wireOp",EDGE,"E0.sketch_text.stroke-16"),sQuery(id+"F0.wireOp",EDGE,"E0.sketch_text.stroke-17"),sQuery(id+"F0.wireOp",EDGE,"E0.sketch_text.stroke-18"),sQuery(id+"F0.wireOp",EDGE,"E0.sketch_text.stroke-19"),sQuery(id+"F0.wireOp",EDGE,"E0.sketch_text.stroke-21"),sQuery(id+"F0.wireOp",EDGE,"E0.sketch_text.stroke-22"),sQuery(id+"F0.wireOp",EDGE,"E0.sketch_text.stroke-23"),sQuery(id+"F0.wireOp",EDGE,"E0.sketch_text.stroke-25"),sQuery(id+"F0.wireOp",EDGE,"E0.sketch_text.stroke-26"),sQuery(id+"F0.wireOp",EDGE,"E0.sketch_text.stroke-27"),sQuery(id+"F0.wireOp",EDGE,"E0.sketch_text.stroke-28"),sQuery(id+"F0.wireOp",EDGE,"E0.sketch_text.stroke-29"),sQuery(id+"F0.wireOp",EDGE,"E0.sketch_text.stroke-30"),sQuery(id+"F0.wireOp",EDGE,"E0.sketch_text.stroke-31"),sQuery(id+"F0.wireOp",EDGE,"E0.sketch_text.stroke-33"),sQuery(id+"F0.wireOp",EDGE,"E0.sketch_text.stroke-34"),sQuery(id+"F0.wireOp",EDGE,"E0.sketch_text.stroke-35"),sQuery(id+"F0.wireOp",EDGE,"E0.sketch_text.stroke-36"),sQuery(id+"F0.wireOp",EDGE,"E0.sketch_text.stroke-37"),sQuery(id+"F0.wireOp",EDGE,"E0.sketch_text.stroke-38"),sQuery(id+"F0.wireOp",EDGE,"E0.sketch_text.stroke-39"),sQuery(id+"F0.wireOp",EDGE,"E0.sketch_text.stroke-40"),sQuery(id+"F0.wireOp",EDGE,"E0.sketch_text.stroke-41"),sQuery(id+"F0.wireOp",EDGE,"E0.sketch_text.stroke-42"),sQuery(id+"F0.wireOp",EDGE,"E0.sketch_text.stroke-43"),sQuery(id+"F0.wireOp",EDGE,"E1.bottom"),sQuery(id+"F0.wireOp",EDGE,"E1.top"),sQuery(id+"F0.wireOp",EDGE,"E6"),sQuery(id+"F0.wireOp",EDGE,"E7"),sQuery(id+"F0.wireOp",EDGE,"E8.MirrorCS"),sQuery(id+"F0.wireOp",EDGE,"E9.MirrorCS")])],"isStart":false})});
            var Q5;
            Q5=makeQuery(id+"F2.boolean.opBoolean","COPY",FACE,{"derivedFrom":makeQuery(id+"F2.opExtrude","CAP_FACE",FACE,{"disambiguationData":[OSD([sQuery(id+"F0.wireOp",EDGE,"63b13505-105a-406d-b1b1-810f40fcbeff.sketch_text.stroke-12"),sQuery(id+"F0.wireOp",EDGE,"63b13505-105a-406d-b1b1-810f40fcbeff.sketch_text.stroke-13"),sQuery(id+"F0.wireOp",EDGE,"63b13505-105a-406d-b1b1-810f40fcbeff.sketch_text.stroke-14"),sQuery(id+"F0.wireOp",EDGE,"63b13505-105a-406d-b1b1-810f40fcbeff.sketch_text.stroke-15"),sQuery(id+"F0.wireOp",EDGE,"63b13505-105a-406d-b1b1-810f40fcbeff.sketch_text.stroke-16"),sQuery(id+"F0.wireOp",EDGE,"63b13505-105a-406d-b1b1-810f40fcbeff.sketch_text.stroke-17"),sQuery(id+"F0.wireOp",EDGE,"63b13505-105a-406d-b1b1-810f40fcbeff.sketch_text.stroke-18"),sQuery(id+"F0.wireOp",EDGE,"63b13505-105a-406d-b1b1-810f40fcbeff.sketch_text.stroke-19"),sQuery(id+"F0.wireOp",EDGE,"63b13505-105a-406d-b1b1-810f40fcbeff.sketch_text.stroke-20"),sQuery(id+"F0.wireOp",EDGE,"63b13505-105a-406d-b1b1-810f40fcbeff.sketch_text.stroke-21"),sQuery(id+"F0.wireOp",EDGE,"63b13505-105a-406d-b1b1-810f40fcbeff.sketch_text.stroke-22"),sQuery(id+"F0.wireOp",EDGE,"63b13505-105a-406d-b1b1-810f40fcbeff.sketch_text.stroke-23"),sQuery(id+"F0.wireOp",EDGE,"63b13505-105a-406d-b1b1-810f40fcbeff.sketch_text.stroke-24"),sQuery(id+"F0.wireOp",EDGE,"63b13505-105a-406d-b1b1-810f40fcbeff.sketch_text.stroke-25"),sQuery(id+"F0.wireOp",EDGE,"63b13505-105a-406d-b1b1-810f40fcbeff.sketch_text.stroke-26"),sQuery(id+"F0.wireOp",EDGE,"63b13505-105a-406d-b1b1-810f40fcbeff.sketch_text.stroke-27"),sQuery(id+"F0.wireOp",EDGE,"63b13505-105a-406d-b1b1-810f40fcbeff.sketch_text.stroke-28")])],"isStart":true})});
            var Q6;
            Q6=makeQuery(id+"F2.boolean.opBoolean","COPY",FACE,{"derivedFrom":makeQuery(id+"F2.opExtrude","CAP_FACE",FACE,{"disambiguationData":[OSD([sQuery(id+"F0.wireOp",EDGE,"63b13505-105a-406d-b1b1-810f40fcbeff.sketch_text.stroke-0"),sQuery(id+"F0.wireOp",EDGE,"63b13505-105a-406d-b1b1-810f40fcbeff.sketch_text.stroke-1"),sQuery(id+"F0.wireOp",EDGE,"63b13505-105a-406d-b1b1-810f40fcbeff.sketch_text.stroke-2"),sQuery(id+"F0.wireOp",EDGE,"63b13505-105a-406d-b1b1-810f40fcbeff.sketch_text.stroke-3"),sQuery(id+"F0.wireOp",EDGE,"63b13505-105a-406d-b1b1-810f40fcbeff.sketch_text.stroke-4"),sQuery(id+"F0.wireOp",EDGE,"63b13505-105a-406d-b1b1-810f40fcbeff.sketch_text.stroke-5"),sQuery(id+"F0.wireOp",EDGE,"63b13505-105a-406d-b1b1-810f40fcbeff.sketch_text.stroke-6"),sQuery(id+"F0.wireOp",EDGE,"63b13505-105a-406d-b1b1-810f40fcbeff.sketch_text.stroke-7"),sQuery(id+"F0.wireOp",EDGE,"63b13505-105a-406d-b1b1-810f40fcbeff.sketch_text.stroke-8"),sQuery(id+"F0.wireOp",EDGE,"63b13505-105a-406d-b1b1-810f40fcbeff.sketch_text.stroke-9"),sQuery(id+"F0.wireOp",EDGE,"63b13505-105a-406d-b1b1-810f40fcbeff.sketch_text.stroke-10"),sQuery(id+"F0.wireOp",EDGE,"63b13505-105a-406d-b1b1-810f40fcbeff.sketch_text.stroke-11")])],"isStart":true})});
            var Q7;
            Q7=makeQuery(id+"F2.boolean.opBoolean","COPY",FACE,{"derivedFrom":makeQuery(id+"F2.opExtrude","CAP_FACE",FACE,{"disambiguationData":[OSD([sQuery(id+"F0.wireOp",EDGE,"63b13505-105a-406d-b1b1-810f40fcbeff.sketch_text.stroke-29"),sQuery(id+"F0.wireOp",EDGE,"63b13505-105a-406d-b1b1-810f40fcbeff.sketch_text.stroke-30"),sQuery(id+"F0.wireOp",EDGE,"63b13505-105a-406d-b1b1-810f40fcbeff.sketch_text.stroke-31"),sQuery(id+"F0.wireOp",EDGE,"63b13505-105a-406d-b1b1-810f40fcbeff.sketch_text.stroke-32"),sQuery(id+"F0.wireOp",EDGE,"63b13505-105a-406d-b1b1-810f40fcbeff.sketch_text.stroke-33"),sQuery(id+"F0.wireOp",EDGE,"63b13505-105a-406d-b1b1-810f40fcbeff.sketch_text.stroke-34"),sQuery(id+"F0.wireOp",EDGE,"63b13505-105a-406d-b1b1-810f40fcbeff.sketch_text.stroke-35"),sQuery(id+"F0.wireOp",EDGE,"63b13505-105a-406d-b1b1-810f40fcbeff.sketch_text.stroke-36"),sQuery(id+"F0.wireOp",EDGE,"63b13505-105a-406d-b1b1-810f40fcbeff.sketch_text.stroke-37"),sQuery(id+"F0.wireOp",EDGE,"63b13505-105a-406d-b1b1-810f40fcbeff.sketch_text.stroke-38"),sQuery(id+"F0.wireOp",EDGE,"63b13505-105a-406d-b1b1-810f40fcbeff.sketch_text.stroke-39"),sQuery(id+"F0.wireOp",EDGE,"63b13505-105a-406d-b1b1-810f40fcbeff.sketch_text.stroke-40"),sQuery(id+"F0.wireOp",EDGE,"63b13505-105a-406d-b1b1-810f40fcbeff.sketch_text.stroke-41"),sQuery(id+"F0.wireOp",EDGE,"63b13505-105a-406d-b1b1-810f40fcbeff.sketch_text.stroke-42"),sQuery(id+"F0.wireOp",EDGE,"63b13505-105a-406d-b1b1-810f40fcbeff.sketch_text.stroke-43"),sQuery(id+"F0.wireOp",EDGE,"63b13505-105a-406d-b1b1-810f40fcbeff.sketch_text.stroke-44"),sQuery(id+"F0.wireOp",EDGE,"63b13505-105a-406d-b1b1-810f40fcbeff.sketch_text.stroke-45")])],"isStart":true})});
            var Q8;
            Q8=makeQuery(id+"F2.boolean.opBoolean","COPY",FACE,{"derivedFrom":makeQuery(id+"F2.opExtrude","CAP_FACE",FACE,{"disambiguationData":[OSD([sQuery(id+"F0.wireOp",EDGE,"63b13505-105a-406d-b1b1-810f40fcbeff.sketch_text.stroke-46"),sQuery(id+"F0.wireOp",EDGE,"63b13505-105a-406d-b1b1-810f40fcbeff.sketch_text.stroke-47"),sQuery(id+"F0.wireOp",EDGE,"63b13505-105a-406d-b1b1-810f40fcbeff.sketch_text.stroke-48"),sQuery(id+"F0.wireOp",EDGE,"63b13505-105a-406d-b1b1-810f40fcbeff.sketch_text.stroke-49"),sQuery(id+"F0.wireOp",EDGE,"63b13505-105a-406d-b1b1-810f40fcbeff.sketch_text.stroke-50"),sQuery(id+"F0.wireOp",EDGE,"63b13505-105a-406d-b1b1-810f40fcbeff.sketch_text.stroke-51"),sQuery(id+"F0.wireOp",EDGE,"63b13505-105a-406d-b1b1-810f40fcbeff.sketch_text.stroke-52"),sQuery(id+"F0.wireOp",EDGE,"63b13505-105a-406d-b1b1-810f40fcbeff.sketch_text.stroke-53"),sQuery(id+"F0.wireOp",EDGE,"63b13505-105a-406d-b1b1-810f40fcbeff.sketch_text.stroke-54"),sQuery(id+"F0.wireOp",EDGE,"63b13505-105a-406d-b1b1-810f40fcbeff.sketch_text.stroke-55"),sQuery(id+"F0.wireOp",EDGE,"63b13505-105a-406d-b1b1-810f40fcbeff.sketch_text.stroke-56"),sQuery(id+"F0.wireOp",EDGE,"63b13505-105a-406d-b1b1-810f40fcbeff.sketch_text.stroke-57"),sQuery(id+"F0.wireOp",EDGE,"63b13505-105a-406d-b1b1-810f40fcbeff.sketch_text.stroke-58"),sQuery(id+"F0.wireOp",EDGE,"63b13505-105a-406d-b1b1-810f40fcbeff.sketch_text.stroke-59"),sQuery(id+"F0.wireOp",EDGE,"63b13505-105a-406d-b1b1-810f40fcbeff.sketch_text.stroke-60"),sQuery(id+"F0.wireOp",EDGE,"63b13505-105a-406d-b1b1-810f40fcbeff.sketch_text.stroke-61"),sQuery(id+"F0.wireOp",EDGE,"63b13505-105a-406d-b1b1-810f40fcbeff.sketch_text.stroke-62"),sQuery(id+"F0.wireOp",EDGE,"63b13505-105a-406d-b1b1-810f40fcbeff.sketch_text.stroke-63"),sQuery(id+"F0.wireOp",EDGE,"63b13505-105a-406d-b1b1-810f40fcbeff.sketch_text.stroke-64"),sQuery(id+"F0.wireOp",EDGE,"63b13505-105a-406d-b1b1-810f40fcbeff.sketch_text.stroke-65"),sQuery(id+"F0.wireOp",EDGE,"63b13505-105a-406d-b1b1-810f40fcbeff.sketch_text.stroke-66"),sQuery(id+"F0.wireOp",EDGE,"63b13505-105a-406d-b1b1-810f40fcbeff.sketch_text.stroke-67"),sQuery(id+"F0.wireOp",EDGE,"63b13505-105a-406d-b1b1-810f40fcbeff.sketch_text.stroke-68"),sQuery(id+"F0.wireOp",EDGE,"63b13505-105a-406d-b1b1-810f40fcbeff.sketch_text.stroke-69"),sQuery(id+"F0.wireOp",EDGE,"63b13505-105a-406d-b1b1-810f40fcbeff.sketch_text.stroke-70"),sQuery(id+"F0.wireOp",EDGE,"63b13505-105a-406d-b1b1-810f40fcbeff.sketch_text.stroke-71"),sQuery(id+"F0.wireOp",EDGE,"63b13505-105a-406d-b1b1-810f40fcbeff.sketch_text.stroke-72"),sQuery(id+"F0.wireOp",EDGE,"63b13505-105a-406d-b1b1-810f40fcbeff.sketch_text.stroke-73"),sQuery(id+"F0.wireOp",EDGE,"63b13505-105a-406d-b1b1-810f40fcbeff.sketch_text.stroke-74"),sQuery(id+"F0.wireOp",EDGE,"63b13505-105a-406d-b1b1-810f40fcbeff.sketch_text.stroke-75"),sQuery(id+"F0.wireOp",EDGE,"63b13505-105a-406d-b1b1-810f40fcbeff.sketch_text.stroke-76"),sQuery(id+"F0.wireOp",EDGE,"63b13505-105a-406d-b1b1-810f40fcbeff.sketch_text.stroke-77"),sQuery(id+"F0.wireOp",EDGE,"63b13505-105a-406d-b1b1-810f40fcbeff.sketch_text.stroke-78"),sQuery(id+"F0.wireOp",EDGE,"63b13505-105a-406d-b1b1-810f40fcbeff.sketch_text.stroke-79"),sQuery(id+"F0.wireOp",EDGE,"63b13505-105a-406d-b1b1-810f40fcbeff.sketch_text.stroke-80"),sQuery(id+"F0.wireOp",EDGE,"63b13505-105a-406d-b1b1-810f40fcbeff.sketch_text.stroke-81"),sQuery(id+"F0.wireOp",EDGE,"63b13505-105a-406d-b1b1-810f40fcbeff.sketch_text.stroke-82"),sQuery(id+"F0.wireOp",EDGE,"63b13505-105a-406d-b1b1-810f40fcbeff.sketch_text.stroke-83"),sQuery(id+"F0.wireOp",EDGE,"63b13505-105a-406d-b1b1-810f40fcbeff.sketch_text.stroke-84"),sQuery(id+"F0.wireOp",EDGE,"63b13505-105a-406d-b1b1-810f40fcbeff.sketch_text.stroke-85"),sQuery(id+"F0.wireOp",EDGE,"63b13505-105a-406d-b1b1-810f40fcbeff.sketch_text.stroke-86"),sQuery(id+"F0.wireOp",EDGE,"63b13505-105a-406d-b1b1-810f40fcbeff.sketch_text.stroke-87"),sQuery(id+"F0.wireOp",EDGE,"63b13505-105a-406d-b1b1-810f40fcbeff.sketch_text.stroke-88"),sQuery(id+"F0.wireOp",EDGE,"63b13505-105a-406d-b1b1-810f40fcbeff.sketch_text.stroke-89")])],"isStart":true})});
            var Q9;
            Q9=makeQuery(id+"F2.boolean.opBoolean","SPLIT",FACE,{"disambiguationData":[TD([makeQuery(id+"F2.opExtrude","SWEPT_FACE",FACE,{"disambiguationData":[OSD([sQuery(id+"F0.wireOp",EDGE,"63b13505-105a-406d-b1b1-810f40fcbeff.sketch_text.stroke-104")])]})])],"derivedFrom":makeQuery(id+"F1.opExtrude","CAP_FACE",FACE,{"disambiguationData":[OSD([sQuery(id+"F0.wireOp",EDGE,"E0.sketch_text.stroke-0"),sQuery(id+"F0.wireOp",EDGE,"E0.sketch_text.stroke-1"),sQuery(id+"F0.wireOp",EDGE,"E0.sketch_text.stroke-2"),sQuery(id+"F0.wireOp",EDGE,"E0.sketch_text.stroke-3"),sQuery(id+"F0.wireOp",EDGE,"E0.sketch_text.stroke-4"),sQuery(id+"F0.wireOp",EDGE,"E0.sketch_text.stroke-6"),sQuery(id+"F0.wireOp",EDGE,"E0.sketch_text.stroke-7"),sQuery(id+"F0.wireOp",EDGE,"E0.sketch_text.stroke-8"),sQuery(id+"F0.wireOp",EDGE,"E0.sketch_text.stroke-9"),sQuery(id+"F0.wireOp",EDGE,"E0.sketch_text.stroke-10"),sQuery(id+"F0.wireOp",EDGE,"E0.sketch_text.stroke-11"),sQuery(id+"F0.wireOp",EDGE,"E0.sketch_text.stroke-12"),sQuery(id+"F0.wireOp",EDGE,"E0.sketch_text.stroke-13"),sQuery(id+"F0.wireOp",EDGE,"E0.sketch_text.stroke-14"),sQuery(id+"F0.wireOp",EDGE,"E0.sketch_text.stroke-15"),sQuery(id+"F0.wireOp",EDGE,"E0.sketch_text.stroke-16"),sQuery(id+"F0.wireOp",EDGE,"E0.sketch_text.stroke-17"),sQuery(id+"F0.wireOp",EDGE,"E0.sketch_text.stroke-18"),sQuery(id+"F0.wireOp",EDGE,"E0.sketch_text.stroke-19"),sQuery(id+"F0.wireOp",EDGE,"E0.sketch_text.stroke-21"),sQuery(id+"F0.wireOp",EDGE,"E0.sketch_text.stroke-22"),sQuery(id+"F0.wireOp",EDGE,"E0.sketch_text.stroke-23"),sQuery(id+"F0.wireOp",EDGE,"E0.sketch_text.stroke-25"),sQuery(id+"F0.wireOp",EDGE,"E0.sketch_text.stroke-26"),sQuery(id+"F0.wireOp",EDGE,"E0.sketch_text.stroke-27"),sQuery(id+"F0.wireOp",EDGE,"E0.sketch_text.stroke-28"),sQuery(id+"F0.wireOp",EDGE,"E0.sketch_text.stroke-29"),sQuery(id+"F0.wireOp",EDGE,"E0.sketch_text.stroke-30"),sQuery(id+"F0.wireOp",EDGE,"E0.sketch_text.stroke-31"),sQuery(id+"F0.wireOp",EDGE,"E0.sketch_text.stroke-33"),sQuery(id+"F0.wireOp",EDGE,"E0.sketch_text.stroke-34"),sQuery(id+"F0.wireOp",EDGE,"E0.sketch_text.stroke-35"),sQuery(id+"F0.wireOp",EDGE,"E0.sketch_text.stroke-36"),sQuery(id+"F0.wireOp",EDGE,"E0.sketch_text.stroke-37"),sQuery(id+"F0.wireOp",EDGE,"E0.sketch_text.stroke-38"),sQuery(id+"F0.wireOp",EDGE,"E0.sketch_text.stroke-39"),sQuery(id+"F0.wireOp",EDGE,"E0.sketch_text.stroke-40"),sQuery(id+"F0.wireOp",EDGE,"E0.sketch_text.stroke-41"),sQuery(id+"F0.wireOp",EDGE,"E0.sketch_text.stroke-42"),sQuery(id+"F0.wireOp",EDGE,"E0.sketch_text.stroke-43"),sQuery(id+"F0.wireOp",EDGE,"E1.bottom"),sQuery(id+"F0.wireOp",EDGE,"E1.top"),sQuery(id+"F0.wireOp",EDGE,"E6"),sQuery(id+"F0.wireOp",EDGE,"E7"),sQuery(id+"F0.wireOp",EDGE,"E8.MirrorCS"),sQuery(id+"F0.wireOp",EDGE,"E9.MirrorCS")])],"isStart":false})});
            var Q10;
            Q10=makeQuery(id+"F2.boolean.opBoolean","COPY",FACE,{"derivedFrom":makeQuery(id+"F2.opExtrude","CAP_FACE",FACE,{"disambiguationData":[OSD([sQuery(id+"F0.wireOp",EDGE,"63b13505-105a-406d-b1b1-810f40fcbeff.sketch_text.stroke-90"),sQuery(id+"F0.wireOp",EDGE,"63b13505-105a-406d-b1b1-810f40fcbeff.sketch_text.stroke-91"),sQuery(id+"F0.wireOp",EDGE,"63b13505-105a-406d-b1b1-810f40fcbeff.sketch_text.stroke-92"),sQuery(id+"F0.wireOp",EDGE,"63b13505-105a-406d-b1b1-810f40fcbeff.sketch_text.stroke-93"),sQuery(id+"F0.wireOp",EDGE,"63b13505-105a-406d-b1b1-810f40fcbeff.sketch_text.stroke-94"),sQuery(id+"F0.wireOp",EDGE,"63b13505-105a-406d-b1b1-810f40fcbeff.sketch_text.stroke-95"),sQuery(id+"F0.wireOp",EDGE,"63b13505-105a-406d-b1b1-810f40fcbeff.sketch_text.stroke-96"),sQuery(id+"F0.wireOp",EDGE,"63b13505-105a-406d-b1b1-810f40fcbeff.sketch_text.stroke-97"),sQuery(id+"F0.wireOp",EDGE,"63b13505-105a-406d-b1b1-810f40fcbeff.sketch_text.stroke-98"),sQuery(id+"F0.wireOp",EDGE,"63b13505-105a-406d-b1b1-810f40fcbeff.sketch_text.stroke-99"),sQuery(id+"F0.wireOp",EDGE,"63b13505-105a-406d-b1b1-810f40fcbeff.sketch_text.stroke-100"),sQuery(id+"F0.wireOp",EDGE,"63b13505-105a-406d-b1b1-810f40fcbeff.sketch_text.stroke-101"),sQuery(id+"F0.wireOp",EDGE,"63b13505-105a-406d-b1b1-810f40fcbeff.sketch_text.stroke-102"),sQuery(id+"F0.wireOp",EDGE,"63b13505-105a-406d-b1b1-810f40fcbeff.sketch_text.stroke-103"),sQuery(id+"F0.wireOp",EDGE,"63b13505-105a-406d-b1b1-810f40fcbeff.sketch_text.stroke-104"),sQuery(id+"F0.wireOp",EDGE,"63b13505-105a-406d-b1b1-810f40fcbeff.sketch_text.stroke-105"),sQuery(id+"F0.wireOp",EDGE,"63b13505-105a-406d-b1b1-810f40fcbeff.sketch_text.stroke-106"),sQuery(id+"F0.wireOp",EDGE,"63b13505-105a-406d-b1b1-810f40fcbeff.sketch_text.stroke-107"),sQuery(id+"F0.wireOp",EDGE,"63b13505-105a-406d-b1b1-810f40fcbeff.sketch_text.stroke-108")])],"isStart":true})});
            var Q11;
            Q11=makeQuery(id+"F2.boolean.opBoolean","COPY",FACE,{"derivedFrom":makeQuery(id+"F2.opExtrude","CAP_FACE",FACE,{"disambiguationData":[OSD([sQuery(id+"F0.wireOp",EDGE,"63b13505-105a-406d-b1b1-810f40fcbeff.sketch_text.stroke-109"),sQuery(id+"F0.wireOp",EDGE,"63b13505-105a-406d-b1b1-810f40fcbeff.sketch_text.stroke-110"),sQuery(id+"F0.wireOp",EDGE,"63b13505-105a-406d-b1b1-810f40fcbeff.sketch_text.stroke-111"),sQuery(id+"F0.wireOp",EDGE,"63b13505-105a-406d-b1b1-810f40fcbeff.sketch_text.stroke-112"),sQuery(id+"F0.wireOp",EDGE,"63b13505-105a-406d-b1b1-810f40fcbeff.sketch_text.stroke-113"),sQuery(id+"F0.wireOp",EDGE,"63b13505-105a-406d-b1b1-810f40fcbeff.sketch_text.stroke-114"),sQuery(id+"F0.wireOp",EDGE,"63b13505-105a-406d-b1b1-810f40fcbeff.sketch_text.stroke-115"),sQuery(id+"F0.wireOp",EDGE,"63b13505-105a-406d-b1b1-810f40fcbeff.sketch_text.stroke-116"),sQuery(id+"F0.wireOp",EDGE,"63b13505-105a-406d-b1b1-810f40fcbeff.sketch_text.stroke-117"),sQuery(id+"F0.wireOp",EDGE,"63b13505-105a-406d-b1b1-810f40fcbeff.sketch_text.stroke-118"),sQuery(id+"F0.wireOp",EDGE,"63b13505-105a-406d-b1b1-810f40fcbeff.sketch_text.stroke-119"),sQuery(id+"F0.wireOp",EDGE,"63b13505-105a-406d-b1b1-810f40fcbeff.sketch_text.stroke-120"),sQuery(id+"F0.wireOp",EDGE,"63b13505-105a-406d-b1b1-810f40fcbeff.sketch_text.stroke-121"),sQuery(id+"F0.wireOp",EDGE,"63b13505-105a-406d-b1b1-810f40fcbeff.sketch_text.stroke-122"),sQuery(id+"F0.wireOp",EDGE,"63b13505-105a-406d-b1b1-810f40fcbeff.sketch_text.stroke-123"),sQuery(id+"F0.wireOp",EDGE,"63b13505-105a-406d-b1b1-810f40fcbeff.sketch_text.stroke-124"),sQuery(id+"F0.wireOp",EDGE,"63b13505-105a-406d-b1b1-810f40fcbeff.sketch_text.stroke-125")])],"isStart":true})});
            var Q12;
            Q12=makeQuery(id+"F2.boolean.opBoolean","SPLIT",FACE,{"disambiguationData":[TD([makeQuery(id+"F2.opExtrude","SWEPT_FACE",FACE,{"disambiguationData":[OSD([sQuery(id+"F0.wireOp",EDGE,"63b13505-105a-406d-b1b1-810f40fcbeff.sketch_text.stroke-141")])]})])],"derivedFrom":makeQuery(id+"F1.opExtrude","CAP_FACE",FACE,{"disambiguationData":[OSD([sQuery(id+"F0.wireOp",EDGE,"E0.sketch_text.stroke-0"),sQuery(id+"F0.wireOp",EDGE,"E0.sketch_text.stroke-1"),sQuery(id+"F0.wireOp",EDGE,"E0.sketch_text.stroke-2"),sQuery(id+"F0.wireOp",EDGE,"E0.sketch_text.stroke-3"),sQuery(id+"F0.wireOp",EDGE,"E0.sketch_text.stroke-4"),sQuery(id+"F0.wireOp",EDGE,"E0.sketch_text.stroke-6"),sQuery(id+"F0.wireOp",EDGE,"E0.sketch_text.stroke-7"),sQuery(id+"F0.wireOp",EDGE,"E0.sketch_text.stroke-8"),sQuery(id+"F0.wireOp",EDGE,"E0.sketch_text.stroke-9"),sQuery(id+"F0.wireOp",EDGE,"E0.sketch_text.stroke-10"),sQuery(id+"F0.wireOp",EDGE,"E0.sketch_text.stroke-11"),sQuery(id+"F0.wireOp",EDGE,"E0.sketch_text.stroke-12"),sQuery(id+"F0.wireOp",EDGE,"E0.sketch_text.stroke-13"),sQuery(id+"F0.wireOp",EDGE,"E0.sketch_text.stroke-14"),sQuery(id+"F0.wireOp",EDGE,"E0.sketch_text.stroke-15"),sQuery(id+"F0.wireOp",EDGE,"E0.sketch_text.stroke-16"),sQuery(id+"F0.wireOp",EDGE,"E0.sketch_text.stroke-17"),sQuery(id+"F0.wireOp",EDGE,"E0.sketch_text.stroke-18"),sQuery(id+"F0.wireOp",EDGE,"E0.sketch_text.stroke-19"),sQuery(id+"F0.wireOp",EDGE,"E0.sketch_text.stroke-21"),sQuery(id+"F0.wireOp",EDGE,"E0.sketch_text.stroke-22"),sQuery(id+"F0.wireOp",EDGE,"E0.sketch_text.stroke-23"),sQuery(id+"F0.wireOp",EDGE,"E0.sketch_text.stroke-25"),sQuery(id+"F0.wireOp",EDGE,"E0.sketch_text.stroke-26"),sQuery(id+"F0.wireOp",EDGE,"E0.sketch_text.stroke-27"),sQuery(id+"F0.wireOp",EDGE,"E0.sketch_text.stroke-28"),sQuery(id+"F0.wireOp",EDGE,"E0.sketch_text.stroke-29"),sQuery(id+"F0.wireOp",EDGE,"E0.sketch_text.stroke-30"),sQuery(id+"F0.wireOp",EDGE,"E0.sketch_text.stroke-31"),sQuery(id+"F0.wireOp",EDGE,"E0.sketch_text.stroke-33"),sQuery(id+"F0.wireOp",EDGE,"E0.sketch_text.stroke-34"),sQuery(id+"F0.wireOp",EDGE,"E0.sketch_text.stroke-35"),sQuery(id+"F0.wireOp",EDGE,"E0.sketch_text.stroke-36"),sQuery(id+"F0.wireOp",EDGE,"E0.sketch_text.stroke-37"),sQuery(id+"F0.wireOp",EDGE,"E0.sketch_text.stroke-38"),sQuery(id+"F0.wireOp",EDGE,"E0.sketch_text.stroke-39"),sQuery(id+"F0.wireOp",EDGE,"E0.sketch_text.stroke-40"),sQuery(id+"F0.wireOp",EDGE,"E0.sketch_text.stroke-41"),sQuery(id+"F0.wireOp",EDGE,"E0.sketch_text.stroke-42"),sQuery(id+"F0.wireOp",EDGE,"E0.sketch_text.stroke-43"),sQuery(id+"F0.wireOp",EDGE,"E1.bottom"),sQuery(id+"F0.wireOp",EDGE,"E1.top"),sQuery(id+"F0.wireOp",EDGE,"E6"),sQuery(id+"F0.wireOp",EDGE,"E7"),sQuery(id+"F0.wireOp",EDGE,"E8.MirrorCS"),sQuery(id+"F0.wireOp",EDGE,"E9.MirrorCS")])],"isStart":false})});
            var Q13;
            Q13=makeQuery(id+"F2.boolean.opBoolean","SPLIT",FACE,{"disambiguationData":[TD([makeQuery(id+"F2.opExtrude","SWEPT_FACE",FACE,{"disambiguationData":[OSD([sQuery(id+"F0.wireOp",EDGE,"63b13505-105a-406d-b1b1-810f40fcbeff.sketch_text.stroke-159")])]})])],"derivedFrom":makeQuery(id+"F1.opExtrude","CAP_FACE",FACE,{"disambiguationData":[OSD([sQuery(id+"F0.wireOp",EDGE,"E0.sketch_text.stroke-0"),sQuery(id+"F0.wireOp",EDGE,"E0.sketch_text.stroke-1"),sQuery(id+"F0.wireOp",EDGE,"E0.sketch_text.stroke-2"),sQuery(id+"F0.wireOp",EDGE,"E0.sketch_text.stroke-3"),sQuery(id+"F0.wireOp",EDGE,"E0.sketch_text.stroke-4"),sQuery(id+"F0.wireOp",EDGE,"E0.sketch_text.stroke-6"),sQuery(id+"F0.wireOp",EDGE,"E0.sketch_text.stroke-7"),sQuery(id+"F0.wireOp",EDGE,"E0.sketch_text.stroke-8"),sQuery(id+"F0.wireOp",EDGE,"E0.sketch_text.stroke-9"),sQuery(id+"F0.wireOp",EDGE,"E0.sketch_text.stroke-10"),sQuery(id+"F0.wireOp",EDGE,"E0.sketch_text.stroke-11"),sQuery(id+"F0.wireOp",EDGE,"E0.sketch_text.stroke-12"),sQuery(id+"F0.wireOp",EDGE,"E0.sketch_text.stroke-13"),sQuery(id+"F0.wireOp",EDGE,"E0.sketch_text.stroke-14"),sQuery(id+"F0.wireOp",EDGE,"E0.sketch_text.stroke-15"),sQuery(id+"F0.wireOp",EDGE,"E0.sketch_text.stroke-16"),sQuery(id+"F0.wireOp",EDGE,"E0.sketch_text.stroke-17"),sQuery(id+"F0.wireOp",EDGE,"E0.sketch_text.stroke-18"),sQuery(id+"F0.wireOp",EDGE,"E0.sketch_text.stroke-19"),sQuery(id+"F0.wireOp",EDGE,"E0.sketch_text.stroke-21"),sQuery(id+"F0.wireOp",EDGE,"E0.sketch_text.stroke-22"),sQuery(id+"F0.wireOp",EDGE,"E0.sketch_text.stroke-23"),sQuery(id+"F0.wireOp",EDGE,"E0.sketch_text.stroke-25"),sQuery(id+"F0.wireOp",EDGE,"E0.sketch_text.stroke-26"),sQuery(id+"F0.wireOp",EDGE,"E0.sketch_text.stroke-27"),sQuery(id+"F0.wireOp",EDGE,"E0.sketch_text.stroke-28"),sQuery(id+"F0.wireOp",EDGE,"E0.sketch_text.stroke-29"),sQuery(id+"F0.wireOp",EDGE,"E0.sketch_text.stroke-30"),sQuery(id+"F0.wireOp",EDGE,"E0.sketch_text.stroke-31"),sQuery(id+"F0.wireOp",EDGE,"E0.sketch_text.stroke-33"),sQuery(id+"F0.wireOp",EDGE,"E0.sketch_text.stroke-34"),sQuery(id+"F0.wireOp",EDGE,"E0.sketch_text.stroke-35"),sQuery(id+"F0.wireOp",EDGE,"E0.sketch_text.stroke-36"),sQuery(id+"F0.wireOp",EDGE,"E0.sketch_text.stroke-37"),sQuery(id+"F0.wireOp",EDGE,"E0.sketch_text.stroke-38"),sQuery(id+"F0.wireOp",EDGE,"E0.sketch_text.stroke-39"),sQuery(id+"F0.wireOp",EDGE,"E0.sketch_text.stroke-40"),sQuery(id+"F0.wireOp",EDGE,"E0.sketch_text.stroke-41"),sQuery(id+"F0.wireOp",EDGE,"E0.sketch_text.stroke-42"),sQuery(id+"F0.wireOp",EDGE,"E0.sketch_text.stroke-43"),sQuery(id+"F0.wireOp",EDGE,"E1.bottom"),sQuery(id+"F0.wireOp",EDGE,"E1.top"),sQuery(id+"F0.wireOp",EDGE,"E6"),sQuery(id+"F0.wireOp",EDGE,"E7"),sQuery(id+"F0.wireOp",EDGE,"E8.MirrorCS"),sQuery(id+"F0.wireOp",EDGE,"E9.MirrorCS")])],"isStart":false})});
            var Q14;
            Q14=makeQuery(id+"F2.boolean.opBoolean","SPLIT",FACE,{"disambiguationData":[TD([makeQuery(id+"F2.opExtrude","SWEPT_FACE",FACE,{"disambiguationData":[OSD([sQuery(id+"F0.wireOp",EDGE,"63b13505-105a-406d-b1b1-810f40fcbeff.sketch_text.stroke-176")])]})])],"derivedFrom":makeQuery(id+"F1.opExtrude","CAP_FACE",FACE,{"disambiguationData":[OSD([sQuery(id+"F0.wireOp",EDGE,"E0.sketch_text.stroke-0"),sQuery(id+"F0.wireOp",EDGE,"E0.sketch_text.stroke-1"),sQuery(id+"F0.wireOp",EDGE,"E0.sketch_text.stroke-2"),sQuery(id+"F0.wireOp",EDGE,"E0.sketch_text.stroke-3"),sQuery(id+"F0.wireOp",EDGE,"E0.sketch_text.stroke-4"),sQuery(id+"F0.wireOp",EDGE,"E0.sketch_text.stroke-6"),sQuery(id+"F0.wireOp",EDGE,"E0.sketch_text.stroke-7"),sQuery(id+"F0.wireOp",EDGE,"E0.sketch_text.stroke-8"),sQuery(id+"F0.wireOp",EDGE,"E0.sketch_text.stroke-9"),sQuery(id+"F0.wireOp",EDGE,"E0.sketch_text.stroke-10"),sQuery(id+"F0.wireOp",EDGE,"E0.sketch_text.stroke-11"),sQuery(id+"F0.wireOp",EDGE,"E0.sketch_text.stroke-12"),sQuery(id+"F0.wireOp",EDGE,"E0.sketch_text.stroke-13"),sQuery(id+"F0.wireOp",EDGE,"E0.sketch_text.stroke-14"),sQuery(id+"F0.wireOp",EDGE,"E0.sketch_text.stroke-15"),sQuery(id+"F0.wireOp",EDGE,"E0.sketch_text.stroke-16"),sQuery(id+"F0.wireOp",EDGE,"E0.sketch_text.stroke-17"),sQuery(id+"F0.wireOp",EDGE,"E0.sketch_text.stroke-18"),sQuery(id+"F0.wireOp",EDGE,"E0.sketch_text.stroke-19"),sQuery(id+"F0.wireOp",EDGE,"E0.sketch_text.stroke-21"),sQuery(id+"F0.wireOp",EDGE,"E0.sketch_text.stroke-22"),sQuery(id+"F0.wireOp",EDGE,"E0.sketch_text.stroke-23"),sQuery(id+"F0.wireOp",EDGE,"E0.sketch_text.stroke-25"),sQuery(id+"F0.wireOp",EDGE,"E0.sketch_text.stroke-26"),sQuery(id+"F0.wireOp",EDGE,"E0.sketch_text.stroke-27"),sQuery(id+"F0.wireOp",EDGE,"E0.sketch_text.stroke-28"),sQuery(id+"F0.wireOp",EDGE,"E0.sketch_text.stroke-29"),sQuery(id+"F0.wireOp",EDGE,"E0.sketch_text.stroke-30"),sQuery(id+"F0.wireOp",EDGE,"E0.sketch_text.stroke-31"),sQuery(id+"F0.wireOp",EDGE,"E0.sketch_text.stroke-33"),sQuery(id+"F0.wireOp",EDGE,"E0.sketch_text.stroke-34"),sQuery(id+"F0.wireOp",EDGE,"E0.sketch_text.stroke-35"),sQuery(id+"F0.wireOp",EDGE,"E0.sketch_text.stroke-36"),sQuery(id+"F0.wireOp",EDGE,"E0.sketch_text.stroke-37"),sQuery(id+"F0.wireOp",EDGE,"E0.sketch_text.stroke-38"),sQuery(id+"F0.wireOp",EDGE,"E0.sketch_text.stroke-39"),sQuery(id+"F0.wireOp",EDGE,"E0.sketch_text.stroke-40"),sQuery(id+"F0.wireOp",EDGE,"E0.sketch_text.stroke-41"),sQuery(id+"F0.wireOp",EDGE,"E0.sketch_text.stroke-42"),sQuery(id+"F0.wireOp",EDGE,"E0.sketch_text.stroke-43"),sQuery(id+"F0.wireOp",EDGE,"E1.bottom"),sQuery(id+"F0.wireOp",EDGE,"E1.top"),sQuery(id+"F0.wireOp",EDGE,"E6"),sQuery(id+"F0.wireOp",EDGE,"E7"),sQuery(id+"F0.wireOp",EDGE,"E8.MirrorCS"),sQuery(id+"F0.wireOp",EDGE,"E9.MirrorCS")])],"isStart":false})});
            var Q15;
            Q15=makeQuery(id+"F2.boolean.opBoolean","COPY",FACE,{"derivedFrom":makeQuery(id+"F2.opExtrude","CAP_FACE",FACE,{"disambiguationData":[OSD([sQuery(id+"F0.wireOp",EDGE,"63b13505-105a-406d-b1b1-810f40fcbeff.sketch_text.stroke-126"),sQuery(id+"F0.wireOp",EDGE,"63b13505-105a-406d-b1b1-810f40fcbeff.sketch_text.stroke-127"),sQuery(id+"F0.wireOp",EDGE,"63b13505-105a-406d-b1b1-810f40fcbeff.sketch_text.stroke-128"),sQuery(id+"F0.wireOp",EDGE,"63b13505-105a-406d-b1b1-810f40fcbeff.sketch_text.stroke-129"),sQuery(id+"F0.wireOp",EDGE,"63b13505-105a-406d-b1b1-810f40fcbeff.sketch_text.stroke-130"),sQuery(id+"F0.wireOp",EDGE,"63b13505-105a-406d-b1b1-810f40fcbeff.sketch_text.stroke-131"),sQuery(id+"F0.wireOp",EDGE,"63b13505-105a-406d-b1b1-810f40fcbeff.sketch_text.stroke-132"),sQuery(id+"F0.wireOp",EDGE,"63b13505-105a-406d-b1b1-810f40fcbeff.sketch_text.stroke-133"),sQuery(id+"F0.wireOp",EDGE,"63b13505-105a-406d-b1b1-810f40fcbeff.sketch_text.stroke-134"),sQuery(id+"F0.wireOp",EDGE,"63b13505-105a-406d-b1b1-810f40fcbeff.sketch_text.stroke-135"),sQuery(id+"F0.wireOp",EDGE,"63b13505-105a-406d-b1b1-810f40fcbeff.sketch_text.stroke-136"),sQuery(id+"F0.wireOp",EDGE,"63b13505-105a-406d-b1b1-810f40fcbeff.sketch_text.stroke-137"),sQuery(id+"F0.wireOp",EDGE,"63b13505-105a-406d-b1b1-810f40fcbeff.sketch_text.stroke-138"),sQuery(id+"F0.wireOp",EDGE,"63b13505-105a-406d-b1b1-810f40fcbeff.sketch_text.stroke-139"),sQuery(id+"F0.wireOp",EDGE,"63b13505-105a-406d-b1b1-810f40fcbeff.sketch_text.stroke-140"),sQuery(id+"F0.wireOp",EDGE,"63b13505-105a-406d-b1b1-810f40fcbeff.sketch_text.stroke-141"),sQuery(id+"F0.wireOp",EDGE,"63b13505-105a-406d-b1b1-810f40fcbeff.sketch_text.stroke-142"),sQuery(id+"F0.wireOp",EDGE,"63b13505-105a-406d-b1b1-810f40fcbeff.sketch_text.stroke-143"),sQuery(id+"F0.wireOp",EDGE,"63b13505-105a-406d-b1b1-810f40fcbeff.sketch_text.stroke-144"),sQuery(id+"F0.wireOp",EDGE,"63b13505-105a-406d-b1b1-810f40fcbeff.sketch_text.stroke-145"),sQuery(id+"F0.wireOp",EDGE,"63b13505-105a-406d-b1b1-810f40fcbeff.sketch_text.stroke-146"),sQuery(id+"F0.wireOp",EDGE,"63b13505-105a-406d-b1b1-810f40fcbeff.sketch_text.stroke-147"),sQuery(id+"F0.wireOp",EDGE,"63b13505-105a-406d-b1b1-810f40fcbeff.sketch_text.stroke-148"),sQuery(id+"F0.wireOp",EDGE,"63b13505-105a-406d-b1b1-810f40fcbeff.sketch_text.stroke-149")])],"isStart":true})});
            var Q16;
            Q16=makeQuery(id+"F2.boolean.opBoolean","COPY",FACE,{"derivedFrom":makeQuery(id+"F2.opExtrude","CAP_FACE",FACE,{"disambiguationData":[OSD([sQuery(id+"F0.wireOp",EDGE,"63b13505-105a-406d-b1b1-810f40fcbeff.sketch_text.stroke-150"),sQuery(id+"F0.wireOp",EDGE,"63b13505-105a-406d-b1b1-810f40fcbeff.sketch_text.stroke-151"),sQuery(id+"F0.wireOp",EDGE,"63b13505-105a-406d-b1b1-810f40fcbeff.sketch_text.stroke-152"),sQuery(id+"F0.wireOp",EDGE,"63b13505-105a-406d-b1b1-810f40fcbeff.sketch_text.stroke-153"),sQuery(id+"F0.wireOp",EDGE,"63b13505-105a-406d-b1b1-810f40fcbeff.sketch_text.stroke-154"),sQuery(id+"F0.wireOp",EDGE,"63b13505-105a-406d-b1b1-810f40fcbeff.sketch_text.stroke-155"),sQuery(id+"F0.wireOp",EDGE,"63b13505-105a-406d-b1b1-810f40fcbeff.sketch_text.stroke-156"),sQuery(id+"F0.wireOp",EDGE,"63b13505-105a-406d-b1b1-810f40fcbeff.sketch_text.stroke-157"),sQuery(id+"F0.wireOp",EDGE,"63b13505-105a-406d-b1b1-810f40fcbeff.sketch_text.stroke-158"),sQuery(id+"F0.wireOp",EDGE,"63b13505-105a-406d-b1b1-810f40fcbeff.sketch_text.stroke-159"),sQuery(id+"F0.wireOp",EDGE,"63b13505-105a-406d-b1b1-810f40fcbeff.sketch_text.stroke-160"),sQuery(id+"F0.wireOp",EDGE,"63b13505-105a-406d-b1b1-810f40fcbeff.sketch_text.stroke-161"),sQuery(id+"F0.wireOp",EDGE,"63b13505-105a-406d-b1b1-810f40fcbeff.sketch_text.stroke-162"),sQuery(id+"F0.wireOp",EDGE,"63b13505-105a-406d-b1b1-810f40fcbeff.sketch_text.stroke-163"),sQuery(id+"F0.wireOp",EDGE,"63b13505-105a-406d-b1b1-810f40fcbeff.sketch_text.stroke-164"),sQuery(id+"F0.wireOp",EDGE,"63b13505-105a-406d-b1b1-810f40fcbeff.sketch_text.stroke-165"),sQuery(id+"F0.wireOp",EDGE,"63b13505-105a-406d-b1b1-810f40fcbeff.sketch_text.stroke-166")])],"isStart":true})});
            var Q17;
            Q17=makeQuery(id+"F2.boolean.opBoolean","COPY",FACE,{"derivedFrom":makeQuery(id+"F2.opExtrude","CAP_FACE",FACE,{"disambiguationData":[OSD([sQuery(id+"F0.wireOp",EDGE,"63b13505-105a-406d-b1b1-810f40fcbeff.sketch_text.stroke-167"),sQuery(id+"F0.wireOp",EDGE,"63b13505-105a-406d-b1b1-810f40fcbeff.sketch_text.stroke-168"),sQuery(id+"F0.wireOp",EDGE,"63b13505-105a-406d-b1b1-810f40fcbeff.sketch_text.stroke-169"),sQuery(id+"F0.wireOp",EDGE,"63b13505-105a-406d-b1b1-810f40fcbeff.sketch_text.stroke-170"),sQuery(id+"F0.wireOp",EDGE,"63b13505-105a-406d-b1b1-810f40fcbeff.sketch_text.stroke-171"),sQuery(id+"F0.wireOp",EDGE,"63b13505-105a-406d-b1b1-810f40fcbeff.sketch_text.stroke-172"),sQuery(id+"F0.wireOp",EDGE,"63b13505-105a-406d-b1b1-810f40fcbeff.sketch_text.stroke-173"),sQuery(id+"F0.wireOp",EDGE,"63b13505-105a-406d-b1b1-810f40fcbeff.sketch_text.stroke-174"),sQuery(id+"F0.wireOp",EDGE,"63b13505-105a-406d-b1b1-810f40fcbeff.sketch_text.stroke-175"),sQuery(id+"F0.wireOp",EDGE,"63b13505-105a-406d-b1b1-810f40fcbeff.sketch_text.stroke-176"),sQuery(id+"F0.wireOp",EDGE,"63b13505-105a-406d-b1b1-810f40fcbeff.sketch_text.stroke-177"),sQuery(id+"F0.wireOp",EDGE,"63b13505-105a-406d-b1b1-810f40fcbeff.sketch_text.stroke-178"),sQuery(id+"F0.wireOp",EDGE,"63b13505-105a-406d-b1b1-810f40fcbeff.sketch_text.stroke-179"),sQuery(id+"F0.wireOp",EDGE,"63b13505-105a-406d-b1b1-810f40fcbeff.sketch_text.stroke-180"),sQuery(id+"F0.wireOp",EDGE,"63b13505-105a-406d-b1b1-810f40fcbeff.sketch_text.stroke-181"),sQuery(id+"F0.wireOp",EDGE,"63b13505-105a-406d-b1b1-810f40fcbeff.sketch_text.stroke-182"),sQuery(id+"F0.wireOp",EDGE,"63b13505-105a-406d-b1b1-810f40fcbeff.sketch_text.stroke-183")])],"isStart":true})});
            var Q18;
            Q18=makeQuery(id+"F2.boolean.opBoolean","COPY",FACE,{"derivedFrom":makeQuery(id+"F2.opExtrude","CAP_FACE",FACE,{"disambiguationData":[OSD([sQuery(id+"F0.wireOp",EDGE,"63b13505-105a-406d-b1b1-810f40fcbeff.sketch_text.stroke-184"),sQuery(id+"F0.wireOp",EDGE,"63b13505-105a-406d-b1b1-810f40fcbeff.sketch_text.stroke-185"),sQuery(id+"F0.wireOp",EDGE,"63b13505-105a-406d-b1b1-810f40fcbeff.sketch_text.stroke-186"),sQuery(id+"F0.wireOp",EDGE,"63b13505-105a-406d-b1b1-810f40fcbeff.sketch_text.stroke-187"),sQuery(id+"F0.wireOp",EDGE,"63b13505-105a-406d-b1b1-810f40fcbeff.sketch_text.stroke-188"),sQuery(id+"F0.wireOp",EDGE,"63b13505-105a-406d-b1b1-810f40fcbeff.sketch_text.stroke-189"),sQuery(id+"F0.wireOp",EDGE,"63b13505-105a-406d-b1b1-810f40fcbeff.sketch_text.stroke-190"),sQuery(id+"F0.wireOp",EDGE,"63b13505-105a-406d-b1b1-810f40fcbeff.sketch_text.stroke-191"),sQuery(id+"F0.wireOp",EDGE,"63b13505-105a-406d-b1b1-810f40fcbeff.sketch_text.stroke-192"),sQuery(id+"F0.wireOp",EDGE,"63b13505-105a-406d-b1b1-810f40fcbeff.sketch_text.stroke-193"),sQuery(id+"F0.wireOp",EDGE,"63b13505-105a-406d-b1b1-810f40fcbeff.sketch_text.stroke-194"),sQuery(id+"F0.wireOp",EDGE,"63b13505-105a-406d-b1b1-810f40fcbeff.sketch_text.stroke-195"),sQuery(id+"F0.wireOp",EDGE,"63b13505-105a-406d-b1b1-810f40fcbeff.sketch_text.stroke-196")])],"isStart":true})});
            var Q19;
            Q19=makeQuery(id+"F2.boolean.opBoolean","COPY",FACE,{"derivedFrom":makeQuery(id+"F2.opExtrude","CAP_FACE",FACE,{"disambiguationData":[OSD([sQuery(id+"F0.wireOp",EDGE,"63b13505-105a-406d-b1b1-810f40fcbeff.sketch_text.stroke-197"),sQuery(id+"F0.wireOp",EDGE,"63b13505-105a-406d-b1b1-810f40fcbeff.sketch_text.stroke-198"),sQuery(id+"F0.wireOp",EDGE,"63b13505-105a-406d-b1b1-810f40fcbeff.sketch_text.stroke-199"),sQuery(id+"F0.wireOp",EDGE,"63b13505-105a-406d-b1b1-810f40fcbeff.sketch_text.stroke-200"),sQuery(id+"F0.wireOp",EDGE,"63b13505-105a-406d-b1b1-810f40fcbeff.sketch_text.stroke-201"),sQuery(id+"F0.wireOp",EDGE,"63b13505-105a-406d-b1b1-810f40fcbeff.sketch_text.stroke-202"),sQuery(id+"F0.wireOp",EDGE,"63b13505-105a-406d-b1b1-810f40fcbeff.sketch_text.stroke-203"),sQuery(id+"F0.wireOp",EDGE,"63b13505-105a-406d-b1b1-810f40fcbeff.sketch_text.stroke-204"),sQuery(id+"F0.wireOp",EDGE,"63b13505-105a-406d-b1b1-810f40fcbeff.sketch_text.stroke-205"),sQuery(id+"F0.wireOp",EDGE,"63b13505-105a-406d-b1b1-810f40fcbeff.sketch_text.stroke-206"),sQuery(id+"F0.wireOp",EDGE,"63b13505-105a-406d-b1b1-810f40fcbeff.sketch_text.stroke-207"),sQuery(id+"F0.wireOp",EDGE,"63b13505-105a-406d-b1b1-810f40fcbeff.sketch_text.stroke-208"),sQuery(id+"F0.wireOp",EDGE,"63b13505-105a-406d-b1b1-810f40fcbeff.sketch_text.stroke-209"),sQuery(id+"F0.wireOp",EDGE,"63b13505-105a-406d-b1b1-810f40fcbeff.sketch_text.stroke-210"),sQuery(id+"F0.wireOp",EDGE,"63b13505-105a-406d-b1b1-810f40fcbeff.sketch_text.stroke-211"),sQuery(id+"F0.wireOp",EDGE,"63b13505-105a-406d-b1b1-810f40fcbeff.sketch_text.stroke-212"),sQuery(id+"F0.wireOp",EDGE,"63b13505-105a-406d-b1b1-810f40fcbeff.sketch_text.stroke-213")])],"isStart":true})});
            extrude(context, id + "F3", {"entities" : qUnion([Q0, Q1, Q2, Q3, Q4, Q5, Q6, Q7, Q8, Q9, Q10, Q11, Q12, Q13, Q14, Q15, Q16, Q17, Q18, Q19]), "operationType" : NewBodyOperationType.ADD, "depth" : 25.4 * mm, "offsetDistance" : 25.4 * mm});
        }
        {
            var Q0;
            {var subQ0=sQuery(id+"F0.wireOp",EDGE,"E0.sketch_text.stroke-0");Q0=makeQuery(id+"F0.imprint","IMPRINT",FACE,{"disambiguationData":[TD([[makeQuery(id+"F0.imprint","IMPRINT",EDGE,{"derivedFrom":subQ0}),-1.0]])]});}
            var Q1;
            Q1=makeQuery(id+"F0.imprint","IMPRINT",FACE,{"disambiguationData":[TD([[makeQuery(id+"F0.imprint","IMPRINT",EDGE,{"derivedFrom":sQuery(id+"F0.wireOp",EDGE,"E0.sketch_text.stroke-6")}),-1.0]])]});
            var Q2;
            {var subQ1=sQuery(id+"F0.wireOp",EDGE,"E0.sketch_text.stroke-21");Q2=makeQuery(id+"F0.imprint","IMPRINT",FACE,{"disambiguationData":[TD([[makeQuery(id+"F0.imprint","IMPRINT",EDGE,{"derivedFrom":subQ1}),-1.0]])]});}
            var Q3;
            {var subQ0=sQuery(id+"F0.wireOp",EDGE,"E0.sketch_text.stroke-33");Q3=makeQuery(id+"F0.imprint","IMPRINT",FACE,{"disambiguationData":[TD([[makeQuery(id+"F0.imprint","IMPRINT",EDGE,{"derivedFrom":subQ0}),-1.0]])]});}
            extrude(context, id + "F4", {"entities" : qUnion([Q0, Q1, Q2, Q3]), "operationType" : NewBodyOperationType.REMOVE, "depth" : 50.8 * mm, "offsetDistance" : 25.4 * mm, "hasSecondDirection" : true, "secondDirectionOppositeDirection" : false, "secondDirectionDepth" : 38.1 * mm});
        }
        {
            var Q0;
            Q0=makeQuery(id+"F0.imprint","IMPRINT",FACE,{"disambiguationData":[TD([[makeQuery(id+"F0.imprint","IMPRINT",EDGE,{"derivedFrom":sQuery(id+"F0.wireOp",EDGE,"E0.sketch_text.stroke-6")}),-1.0]])]});
            var Q1;
            {var subQ1=sQuery(id+"F0.wireOp",EDGE,"E0.sketch_text.stroke-21");Q1=makeQuery(id+"F0.imprint","IMPRINT",FACE,{"disambiguationData":[TD([[makeQuery(id+"F0.imprint","IMPRINT",EDGE,{"derivedFrom":subQ1}),-1.0]])]});}
            var Q2;
            {var subQ0=sQuery(id+"F0.wireOp",EDGE,"E0.sketch_text.stroke-33");Q2=makeQuery(id+"F0.imprint","IMPRINT",FACE,{"disambiguationData":[TD([[makeQuery(id+"F0.imprint","IMPRINT",EDGE,{"derivedFrom":subQ0}),-1.0]])]});}
            var Q3;
            {var subQ0=sQuery(id+"F0.wireOp",EDGE,"E0.sketch_text.stroke-0");Q3=makeQuery(id+"F0.imprint","IMPRINT",FACE,{"disambiguationData":[TD([[makeQuery(id+"F0.imprint","IMPRINT",EDGE,{"derivedFrom":subQ0}),-1.0]])]});}
            extrude(context, id + "F5", {"entities" : qUnion([Q0, Q1, Q2, Q3]), "operationType" : NewBodyOperationType.REMOVE, "depth" : 12.7 * mm, "offsetDistance" : 25.4 * mm});
        }
    });
